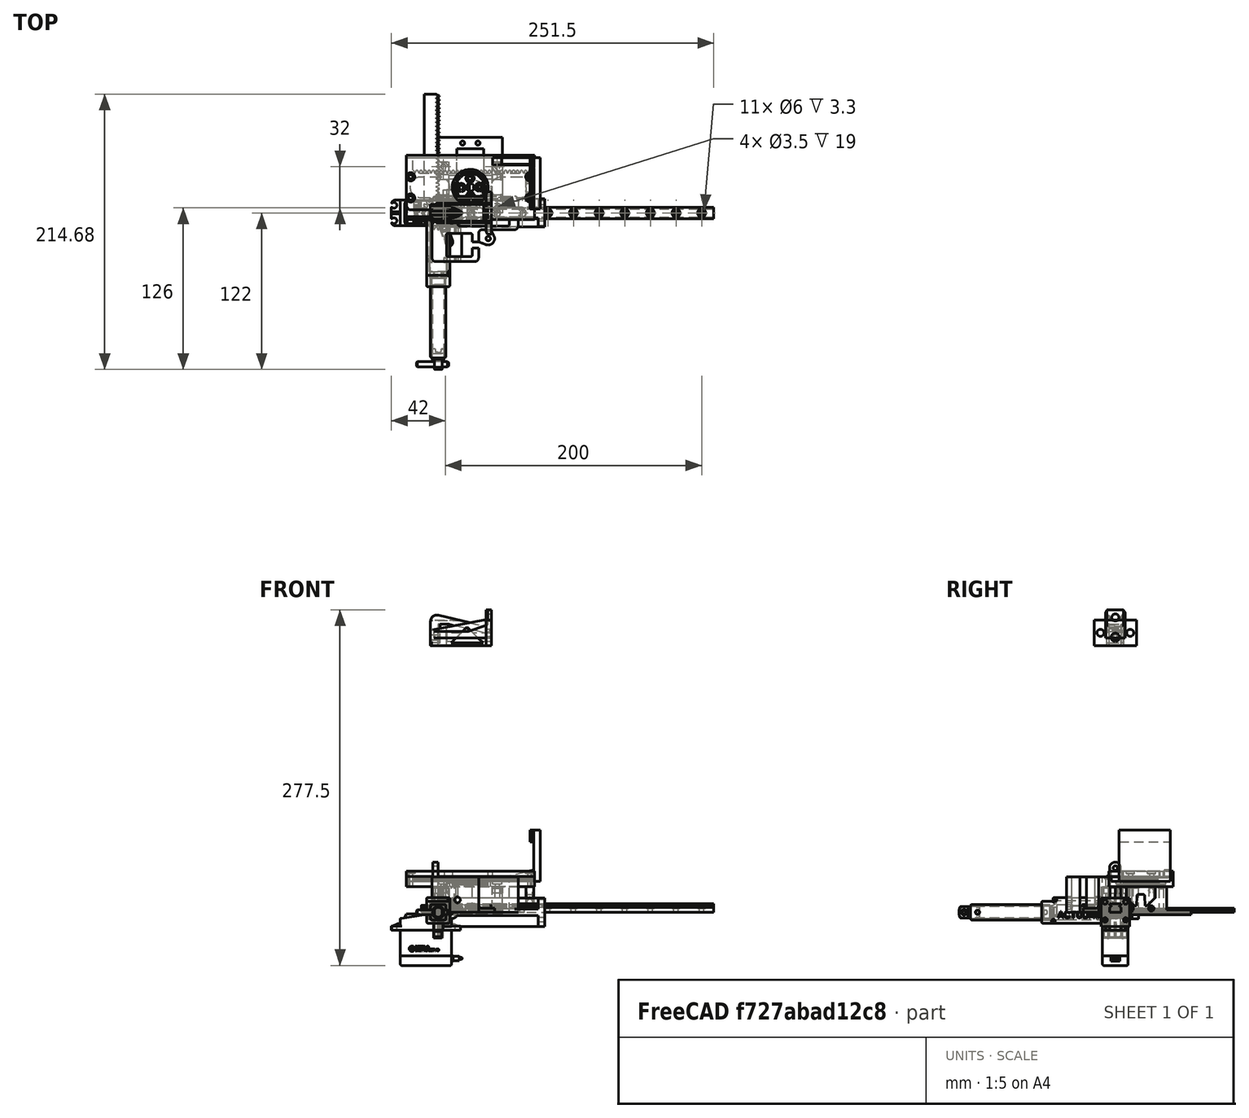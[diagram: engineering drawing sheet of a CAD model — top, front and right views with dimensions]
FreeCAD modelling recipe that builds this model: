
FCSTD DOCUMENT  (FreeCAD 1.0R39285 (Git))
Label: PincePlanche
License: All rights reserved
LicenseURL: https://en.wikipedia.org/wiki/All_rights_reserved
objects: Sketcher::SketchObject×61, PartDesign::Pocket×31, PartDesign::Pad×28, PartDesign::Body×17, App::FeaturePython×11, Part::Feature×9, Part::FeaturePython×8, PartDesign::Mirrored×7, App::Part×6, App::Link×3, PartDesign::Chamfer×2, Assembly::JointGroup×2, PartDesign::Revolution×2, PartDesign::PolarPattern×2, PartDesign::Fillet×2, PartDesign::FeatureBase×2, Assembly::AssemblyObject×2, PartDesign::LinearPattern×1, Spreadsheet::Sheet×1, PartDesign::MultiTransform×1, +2 more types
note: 380 computed .brp shape members not serialized (recipe doc carries the construction recipe); baked Part::Feature solids carry a one-line shape summary decoded from their .brp
EXTERNAL_REF file=Robot_CRLG.FCStd obj=Body073

FEATURE [Part::FeaturePython] InvoluteRack  # WARN: FeaturePython — macro-defined, semantics opaque (R4)
  AttacherType = Attacher::AttachEngine3D
  add_endings = true
  clearance = 0.25
  double_helix = false
  head = 0
  head_fillet = 0
  height = 3
  helix_angle = 0
  module = 1
  num_teeth = 30
  pressure_angle = 20
  properties_from_tool = false
  root_fillet = 0
  simplified = false
  thickness = 9.5
  transverse_pitch = 3.14159
  version = 1.3.0
FEATURE [Part::FeaturePython] InvoluteGear  # WARN: FeaturePython — macro-defined, semantics opaque (R4)
  AttacherType = Attacher::AttachEngine3D
  addendum_diameter = 26
  angular_backlash = 0
  axle_hole = false
  axle_holesize = 10
  backlash = 0
  clearance = 0.25
  double_helix = false
  head = 0
  head_fillet = 0
  height = 5.5
  helix_angle = 0
  module = 1
  num_teeth = 24
  numpoints = 20
  offset_hole = false
  offset_holeoffset = 10
  offset_holesize = 10
  pitch_diameter = 24
  pressure_angle = 20
  properties_from_tool = false
  reversed_backlash = false
  root_diameter = 21.5
  root_fillet = 0
  shift = 0
  simple = false
  transverse_pitch = 3.14159
  traverse_module = 1
  undercut = false
  version = 1.3.0
  expr: angular_backlash = backlash / pitch_diameter * 360 ° / pi
FEATURE [Part::Feature] Part__Feature008002002006397  label="chariot_MGN9-H"
  Placement = pos=(0,0,0) rot=(0.707107,0.707107,0;3.14159rad)
  shape: bbox 8.005 x 20.01 x 40.67 mm, 245 faces, 9 solids (baked)
FEATURE [Sketcher::SketchObject] Sketch031
  ArcFitTolerance = 0
  AttachmentSupport = -> [YZ_Plane013]
  FullyConstrained = true
  MakeInternals = false
  MapMode = 5
  Placement = pos=(0,0,0) rot=(0.57735,0.57735,0.57735;2.0944rad)
  sketch-geometry (4):
    g0: LineSegment StartX=-4.5 StartY=0 StartZ=0 EndX=4.5 EndY=0 EndZ=0
    g1: LineSegment StartX=4.5 StartY=0 StartZ=0 EndX=4.5 EndY=6.5 EndZ=0
    g2: LineSegment StartX=4.5 StartY=6.5 StartZ=0 EndX=-4.5 EndY=6.5 EndZ=0
    g3: LineSegment StartX=-4.5 StartY=6.5 StartZ=0 EndX=-4.5 EndY=0 EndZ=0
  constraints (11):
    c: Coincident(g0,g1)
    c: Coincident(g1,g2)
    c: Coincident(g2,g3)
    c: Coincident(g3,g0)
    c: Horizontal(g0)
    c: Horizontal(g2)
    c: Vertical(g1)
    c: Vertical(g3)
    c: Symmetric(g0,g0,g-1)
    c: DistanceX(g0,g0) = 9  'width'
    c: DistanceY(g1,g1) = 6.5  'height'
FEATURE [PartDesign::Pad] Pad012
  Direction = (1,0,0)
  Length = 215
  Length2 = 10
  Placement = pos=(0,0,0) rot=(0.57735,0.57735,0.57735;2.0944rad)
  Profile = -> Sketch031
  ReferenceAxis = -> Sketch031 [N_Axis]
  Suppressed = false
  Type = 0
  expr: Length = Spreadsheet001.length
FEATURE [Sketcher::SketchObject] Sketch032
  ArcFitTolerance = 0
  AttachmentSupport = -> [YZ_Plane013]
  FullyConstrained = true
  MakeInternals = false
  MapMode = 5
  Placement = pos=(0,0,0) rot=(0.57735,-0.57735,-0.57735;2.0944rad)
  expr: Constraints[13] = 6.5 - 1.8
  expr: Constraints[14] = <<Sketch031>>.Constraints.width / 2 + 0.1 mm
  sketch-geometry (10):
    g0: ArcOfCircle CenterX=-4.6 CenterY=4.7 CenterZ=0 NormalX=0 NormalY=0 NormalZ=1 AngleXU=0 Radius=1 StartAngle=0.25268 EndAngle=6.03051
    g1: LineSegment StartX=-3.63175 StartY=4.95 StartZ=0 EndX=-3.13175 EndY=4.95 EndZ=0
    g2: LineSegment StartX=-3.13175 StartY=4.95 StartZ=0 EndX=-3.13175 EndY=4.45 EndZ=0
    g3: LineSegment StartX=-3.13175 StartY=4.45 StartZ=0 EndX=-3.63175 EndY=4.45 EndZ=0
    g4: LineSegment [constr] StartX=-4.6 StartY=4.7 StartZ=0 EndX=-3.13175 EndY=4.7 EndZ=0
    g5: ArcOfCircle CenterX=4.6 CenterY=4.7 CenterZ=0 NormalX=0 NormalY=0 NormalZ=1 AngleXU=0 Radius=1 StartAngle=3.39427 EndAngle=9.1721
    g6: LineSegment StartX=3.63175 StartY=4.95 StartZ=0 EndX=3.13175 EndY=4.95 EndZ=0
    g7: LineSegment StartX=3.13175 StartY=4.95 StartZ=0 EndX=3.13175 EndY=4.45 EndZ=0
    g8: LineSegment StartX=3.13175 StartY=4.45 StartZ=0 EndX=3.63175 EndY=4.45 EndZ=0
    g9: LineSegment [constr] StartX=4.6 StartY=4.7 StartZ=0 EndX=3.13175 EndY=4.7 EndZ=0
  constraints (29):
    c: Horizontal(g1)
    c: Coincident(g2,g1)
    c: Vertical(g2)
    c: Coincident(g3,g2)
    c: Horizontal(g3)
    c: Coincident(g4,g0)
    c: Horizontal(g4)
    c: Symmetric(g2,g1,g4)
    c: Coincident(g0,g3)
    c: Coincident(g0,g1)
    c: DistanceY(g2,g2) = 0.5
    c: DistanceX(g1,g1) = 0.5
    c: Diameter(g0) = 2
    c: DistanceY(g-1,g0) = 4.7
    c: DistanceX(g0,g-1) = 4.6
    c: Horizontal(g6)
    c: Coincident(g7,g6)
    c: Vertical(g7)
    c: Coincident(g8,g7)
    c: Horizontal(g8)
    c: Coincident(g9,g5)
    c: Horizontal(g9)
    c: Symmetric(g7,g6,g9)
    c: Coincident(g5,g8)
    c: Coincident(g5,g6)
    c: Diameter(g5) = 2
    c: Symmetric(g4,g9,g-2)
    c: Equal(g2,g7)
    c: Equal(g1,g6)
FEATURE [PartDesign::Pocket] Pocket015  label="Balls cut"
  BaseFeature = -> Pad012
  Direction = (1,0,0)
  Length = 5
  Length2 = 5
  Placement = pos=(0,0,0) rot=(0.57735,0.57735,0.57735;2.0944rad)
  Profile = -> Sketch032
  ReferenceAxis = -> Sketch032 [N_Axis]
  Suppressed = false
  Type = 1
FEATURE [Sketcher::SketchObject] Sketch033
  ArcFitTolerance = 0
  AttachmentOffset = pos=(5.5,0,0) rot=(0,0,1;1.5708rad)
  AttachmentSupport = -> [XY_Plane013]
  FullyConstrained = true
  MakeInternals = false
  MapMode = 5
  Placement = pos=(5.5,0,0) rot=(0,0,1;1.5708rad)
  expr: .AttachmentOffset.Base.x = Spreadsheet001.offset
  sketch-geometry (1):
    g0: Circle CenterX=0 CenterY=0 CenterZ=0 NormalX=0 NormalY=0 NormalZ=1 AngleXU=0 Radius=1.75
  constraints (2):
    c: Coincident(g0,g-1)
    c: Diameter(g0) = 3.5
FEATURE [PartDesign::Pocket] Pocket016  label="Screw hole"
  BaseFeature = -> Pocket015
  Direction = (0,0,-1)
  Length = 5
  Length2 = 5
  Midplane = true
  Placement = pos=(0,0,0) rot=(0.57735,0.57735,0.57735;2.0944rad)
  Profile = -> Sketch033
  ReferenceAxis = -> Sketch033 [N_Axis]
  Suppressed = false
  Type = 1
FEATURE [Sketcher::SketchObject] Sketch034
  ArcFitTolerance = 0
  AttachmentOffset = pos=(5.5,0,6.5) rot=(0,0,1;1.5708rad)
  AttachmentSupport = -> [XY_Plane013]
  FullyConstrained = true
  MakeInternals = false
  MapMode = 5
  Placement = pos=(5.5,0,6.5) rot=(0,0,1;1.5708rad)
  expr: .AttachmentOffset.Base.x = Spreadsheet001.offset
  expr: .AttachmentOffset.Base.z = Sketch031.Constraints.height
  sketch-geometry (1):
    g0: Circle CenterX=0 CenterY=0 CenterZ=0 NormalX=0 NormalY=0 NormalZ=1 AngleXU=0 Radius=3
  constraints (2):
    c: Coincident(g0,g-1)
    c: Diameter(g0) = 6
FEATURE [PartDesign::Pocket] Pocket017  label="Screw head cut"
  BaseFeature = -> Pocket016
  Direction = (0,0,-1)
  Length = 3.5
  Length2 = 5
  Placement = pos=(0,0,0) rot=(0.57735,0.57735,0.57735;2.0944rad)
  Profile = -> Sketch034
  ReferenceAxis = -> Sketch034 [N_Axis]
  Suppressed = false
  Type = 0
FEATURE [PartDesign::Chamfer] Chamfer001  label="Chamfer"
  Angle = 45
  Base = -> Pocket017 [Edge47]
  BaseFeature = -> Pocket017
  ChamferType = 0
  FlipDirection = false
  Placement = pos=(0,0,0) rot=(0.57735,0.57735,0.57735;2.0944rad)
  Size = 0.2
  Size2 = 1
  SupportTransform = false
  Suppressed = false
  UseAllEdges = false
FEATURE [PartDesign::LinearPattern] LinearPattern001  label="LinearPattern"
  BaseFeature = -> Chamfer001
  Direction = -> Sketch033 [V_Axis]
  Length = 200
  Mode = 0
  Occurrences = 11
  Offset = 20
  Originals = -> [Pocket016,Pocket017,Chamfer001]
  Placement = pos=(0,0,0) rot=(0.57735,0.57735,0.57735;2.0944rad)
  Reversed = true
  Suppressed = false
  TransformMode = 0
  expr: Length = Spreadsheet001.distance
  expr: Occurrences = Spreadsheet001.holes_number
FEATURE [PartDesign::Body] Body011  label="Hiwin rail MGN9R"
  AllowCompound = false
  Group = -> [Sketch031,Pad012,Sketch032,Pocket015,Sketch033,Pocket016,Sketch034,Pocket017,Chamfer001,LinearPattern001]
  Origin = -> Origin013
  Tip = -> LinearPattern001
FEATURE [Spreadsheet::Sheet] Spreadsheet001  label="Spreadsheet_MGN9"
  cells = A1='Length rail; B1='Длина рельсы, мм; C1(length)=215; A2='Holes distance; B2='Расстояние между отверстиями; C2(holes_distance)=20; A3='Holes number; B3='Количество отверстий; C3(holes_number)==floor((length - min_offset * 2) / holes_distance) + 2; A4='Distance end holes; B4='Расстояние между центрами крайних отверстий; C4(distance)==holes_distance * (holes_number - 1); A5='Offset 1st hole; B5='Позиция 1го отверстия; C5(offset)=5.5; A6='Min offset 1st hole; B6='Минимальное расстояние от края до центра 1го отверстия; C6(min_offset)=9
FEATURE [App::Part] Part002002  label="Hiwin MGN9"
  Group = -> [Body011,Spreadsheet001]
  Origin = -> Origin014
  Placement = pos=(0,0,220) rot=(0,1,0;1.5708rad)
FEATURE [Assembly::JointGroup] Joints001
FEATURE [Part::Feature] Part__Feature008002002006398  label="L16_50MM_BODY_A"
  Placement = pos=(0,-51,0) rot=(0,0,1;0rad)
  shape: bbox 20.08 x 117.7 x 20.17 mm, 719 faces (baked)
FEATURE [Part::Feature] Part__Feature008002002006399  label="L16_50MM_LIFT_A"
  Placement = pos=(0,-51,0) rot=(0,0,1;0rad)
  shape: bbox 10.2 x 71.63 x 9.971 mm, 40 faces (baked)
  expr: .Placement.Base.y = -51 mm - VarSet.Position_verrin
FEATURE [Sketcher::SketchObject] Sketch036
  ArcFitTolerance = 1e-06
  AttachmentSupport = -> [YZ_Plane017]
  FullyConstrained = true
  MakeInternals = false
  MapMode = 5
  Placement = pos=(0,0,0) rot=(0.57735,0.57735,0.57735;2.0944rad)
  sketch-geometry (4):
    g0: LineSegment StartX=-11 StartY=11 StartZ=0 EndX=-11 EndY=-11 EndZ=0
    g1: LineSegment StartX=-11 StartY=-11 StartZ=0 EndX=11 EndY=-11 EndZ=0
    g2: LineSegment StartX=11 StartY=-11 StartZ=0 EndX=11 EndY=11 EndZ=0
    g3: LineSegment StartX=11 StartY=11 StartZ=0 EndX=-11 EndY=11 EndZ=0
  constraints (11):
    c: Coincident(g0,g1)
    c: Coincident(g1,g2)
    c: Coincident(g2,g3)
    c: Coincident(g3,g0)
    c: Vertical(g0)
    c: Vertical(g2)
    c: Horizontal(g1)
    c: Horizontal(g3)
    c: Symmetric(g2,g0,g-1)
    c: DistanceX(g3,g3) = 22
    c: DistanceY(g0,g0) = 22
FEATURE [Sketcher::SketchObject] Sketch037
  ArcFitTolerance = 1e-06
  AttachmentOffset = pos=(0,0,74) rot=(0,0,1;0rad)
  AttachmentSupport = -> [YZ_Plane017]
  FullyConstrained = true
  MakeInternals = false
  MapMode = 5
  Placement = pos=(74,0,0) rot=(0.57735,0.57735,0.57735;2.0944rad)
  sketch-geometry (4):
    g0: LineSegment StartX=-4 StartY=11 StartZ=0 EndX=-4 EndY=-11 EndZ=0
    g1: LineSegment StartX=-4 StartY=-11 StartZ=0 EndX=4 EndY=-11 EndZ=0
    g2: LineSegment StartX=4 StartY=-11 StartZ=0 EndX=4 EndY=11 EndZ=0
    g3: LineSegment StartX=4 StartY=11 StartZ=0 EndX=-4 EndY=11 EndZ=0
  constraints (11):
    c: Coincident(g0,g1)
    c: Coincident(g1,g2)
    c: Coincident(g2,g3)
    c: Coincident(g3,g0)
    c: Vertical(g0)
    c: Vertical(g2)
    c: Horizontal(g1)
    c: Horizontal(g3)
    c: Symmetric(g2,g0,g-1)
    c: DistanceY(g2,g2) = 22
    c: Distance(g1,g1) = 8
FEATURE [Sketcher::SketchObject] Sketch038
  ArcFitTolerance = 1e-06
  AttachmentSupport = -> [YZ_Plane017]
  FullyConstrained = true
  MakeInternals = false
  MapMode = 5
  Placement = pos=(0,0,0) rot=(0.57735,0.57735,0.57735;2.0944rad)
  sketch-geometry (1):
    g0: Circle CenterX=7.5 CenterY=-8 CenterZ=0 NormalX=0 NormalY=0 NormalZ=1 AngleXU=0 Radius=1.75
  constraints (3):
    c: Diameter(g0) = 3.5
    c: DistanceX(g-1,g0) = 7.5
    c: DistanceY(g0,g-1) = 8
FEATURE [PartDesign::Pad] Pad013
  Direction = (1,0,0)
  Length = 6.5
  Length2 = 10
  Placement = pos=(0,0,0) rot=(1,1,1;2.0944rad)
  Profile = -> Sketch036
  ReferenceAxis = -> Sketch036 [N_Axis]
  Suppressed = false
  Type = 0
FEATURE [PartDesign::Pocket] Pocket018
  BaseFeature = -> Pad013
  Direction = (-1,0,0)
  Length = 5
  Length2 = 5
  Midplane = true
  Placement = pos=(0,0,0) rot=(1,1,1;2.0944rad)
  Profile = -> Sketch038
  ReferenceAxis = -> Sketch038 [N_Axis]
  Suppressed = false
  Type = 1
FEATURE [PartDesign::Mirrored] Mirrored002
  MirrorPlane = -> Sketch038 [V_Axis]
  Placement = pos=(0,0,0) rot=(1,1,1;2.0944rad)
  Suppressed = false
  TransformMode = 0
FEATURE [PartDesign::Mirrored] Mirrored003
  MirrorPlane = -> Sketch038 [H_Axis]
  Placement = pos=(0,0,0) rot=(1,1,1;2.0944rad)
  Suppressed = false
  TransformMode = 0
FEATURE [PartDesign::MultiTransform] MultiTransform
  BaseFeature = -> Pocket018
  Originals = -> [Pocket018]
  Placement = pos=(0,0,0) rot=(1,1,1;2.0944rad)
  Suppressed = false
  TransformMode = 0
  Transformations = -> [Mirrored002,Mirrored003]
FEATURE [Sketcher::SketchObject] Sketch040
  ArcFitTolerance = 1e-06
  AttachmentOffset = pos=(0,0,6.5) rot=(0,0,1;0rad)
  AttachmentSupport = -> [YZ_Plane017]
  FullyConstrained = true
  MakeInternals = false
  MapMode = 5
  Placement = pos=(6.5,0,0) rot=(0.57735,0.57735,0.57735;2.0944rad)
  sketch-geometry (4):
    g0: LineSegment StartX=-4 StartY=11 StartZ=0 EndX=-4 EndY=-11 EndZ=0
    g1: LineSegment StartX=-4 StartY=-11 StartZ=0 EndX=4 EndY=-11 EndZ=0
    g2: LineSegment StartX=4 StartY=-11 StartZ=0 EndX=4 EndY=11 EndZ=0
    g3: LineSegment StartX=4 StartY=11 StartZ=0 EndX=-4 EndY=11 EndZ=0
  constraints (11):
    c: Coincident(g0,g1)
    c: Coincident(g1,g2)
    c: Coincident(g2,g3)
    c: Coincident(g3,g0)
    c: Vertical(g0)
    c: Vertical(g2)
    c: Horizontal(g1)
    c: Horizontal(g3)
    c: Symmetric(g2,g0,g-1)
    c: DistanceX(g3,g3) = 8
    c: DistanceY(g2,g2) = 22
FEATURE [PartDesign::AdditiveLoft] AdditiveLoft
  BaseFeature = -> MultiTransform
  Closed = false
  Placement = pos=(0,0,0) rot=(1,1,1;2.0944rad)
  Profile = -> Sketch037
  Ruled = false
  Sections = -> [Sketch040]
  Suppressed = false
FEATURE [Sketcher::SketchObject] Sketch041
  ArcFitTolerance = 1e-06
  AttachmentOffset = pos=(0,1,0) rot=(0,0,1;0rad)
  AttachmentSupport = -> [AdditiveLoft]
  FullyConstrained = true
  MakeInternals = false
  MapMode = 5
  Placement = pos=(74,0,1) rot=(0.57735,0.57735,0.57735;2.0944rad)
  sketch-geometry (8):
    g0: LineSegment StartX=-11 StartY=10 StartZ=0 EndX=-11 EndY=-10 EndZ=0
    g1: LineSegment StartX=-11 StartY=-10 StartZ=0 EndX=11 EndY=-10 EndZ=0
    g2: LineSegment StartX=11 StartY=-10 StartZ=0 EndX=11 EndY=10 EndZ=0
    g3: LineSegment StartX=11 StartY=10 StartZ=0 EndX=-11 EndY=10 EndZ=0
    g4: Circle CenterX=8 CenterY=-7 CenterZ=0 NormalX=0 NormalY=0 NormalZ=1 AngleXU=0 Radius=1.75
    g5: Circle CenterX=-8 CenterY=-7 CenterZ=0 NormalX=0 NormalY=0 NormalZ=1 AngleXU=0 Radius=1.75
    g6: Circle CenterX=8 CenterY=7 CenterZ=0 NormalX=0 NormalY=0 NormalZ=1 AngleXU=0 Radius=1.75
    g7: Circle CenterX=-8 CenterY=7 CenterZ=0 NormalX=0 NormalY=0 NormalZ=1 AngleXU=0 Radius=1.75
  constraints (21):
    c: Coincident(g0,g1)
    c: Coincident(g1,g2)
    c: Coincident(g2,g3)
    c: Coincident(g3,g0)
    c: Vertical(g0)
    c: Vertical(g2)
    c: Horizontal(g1)
    c: Distance(g1,g1) = 22
    c: Symmetric(g0,g1,g-1)
    c: Horizontal(g3)
    c: DistanceY(g2,g2) = 20
    c: Diameter(g4) = 3.5
    c: Diameter(g5) = 3.5
    c: Diameter(g6) = 3.5
    c: Diameter(g7) = 3.5
    c: Symmetric(g7,g4,g-1)
    c: Symmetric(g5,g6,g-1)
    c: Horizontal(g6,g7)
    c: Vertical(g7,g5)
    c: DistanceX(g7,g-1) = 8
    c: DistanceY(g-1,g7) = 7
FEATURE [PartDesign::Pad] Pad014
  BaseFeature = -> AdditiveLoft
  Direction = (1,0,0)
  Length = 5
  Length2 = 10
  Placement = pos=(0,0,0) rot=(1,1,1;2.0944rad)
  Profile = -> Sketch041
  ReferenceAxis = -> Sketch041 [N_Axis]
  Suppressed = false
  Type = 0
FEATURE [Sketcher::SketchObject] Sketch042
  ArcFitTolerance = 1e-06
  AttachmentSupport = -> [XY_Plane019]
  FullyConstrained = true
  MakeInternals = false
  MapMode = 5
  Placement = pos=(0,0,0) rot=(0,1,0;3.14159rad)
  expr: Constraints[36] = 20 mm + VarSet.jeu
  expr: Constraints[37] = 40 mm + VarSet.jeu
  expr: Constraints[72] = 18 mm + VarSet.jeu
  expr: Constraints[73] = 20 mm + VarSet.jeu
  expr: Constraints[86] = 9 mm + VarSet.jeu
  expr: Constraints[87] = 6.5 mm + VarSet.jeu
  sketch-geometry (52):
    g0: LineSegment StartX=-28.5 StartY=-38 StartZ=0 EndX=1.8 EndY=-38 EndZ=0
    g1: LineSegment StartX=4.8 StartY=-35 StartZ=0 EndX=4.8 EndY=10 EndZ=0
    g2: ArcOfCircle CenterX=1.8 CenterY=-35 CenterZ=0 NormalX=0 NormalY=0 NormalZ=1 AngleXU=0 Radius=3 StartAngle=4.71239 EndAngle=6.28319
    g3: ArcOfCircle CenterX=1.8 CenterY=10 CenterZ=0 NormalX=0 NormalY=0 NormalZ=1 AngleXU=0 Radius=3 StartAngle=0 EndAngle=1.5708
    g4: GeomPoint [constr] X=4.8 Y=-38 Z=0
    g5: LineSegment StartX=-59.5 StartY=-13 StartZ=0 EndX=-34.5 EndY=-13 EndZ=0
    g6: LineSegment StartX=1.8 StartY=13 StartZ=0 EndX=-59.5 EndY=13 EndZ=0
    g7: ArcOfCircle CenterX=-59.5 CenterY=10 CenterZ=0 NormalX=0 NormalY=0 NormalZ=1 AngleXU=0 Radius=3 StartAngle=1.5708 EndAngle=3.14159
    g8: ArcOfCircle CenterX=-59.5 CenterY=-10 CenterZ=0 NormalX=0 NormalY=0 NormalZ=1 AngleXU=0 Radius=3 StartAngle=3.14159 EndAngle=4.71239
    g9: LineSegment StartX=-54.575 StartY=-10.075 StartZ=0 EndX=-16.425 EndY=-10.075 EndZ=0
    g10: LineSegment StartX=-15.425 StartY=-9.075 StartZ=0 EndX=-15.425 EndY=9.075 EndZ=0
    g11: LineSegment StartX=-16.425 StartY=10.075 StartZ=0 EndX=-54.575 EndY=10.075 EndZ=0
    g12: ArcOfCircle CenterX=-54.575 CenterY=9.075 CenterZ=0 NormalX=0 NormalY=0 NormalZ=1 AngleXU=0 Radius=1 StartAngle=1.5708 EndAngle=3.14159
    g13: ArcOfCircle CenterX=-54.575 CenterY=-9.075 CenterZ=0 NormalX=0 NormalY=0 NormalZ=1 AngleXU=0 Radius=1 StartAngle=3.14159 EndAngle=4.71239
    g14: ArcOfCircle CenterX=-16.425 CenterY=-9.075 CenterZ=0 NormalX=0 NormalY=0 NormalZ=1 AngleXU=0 Radius=1 StartAngle=4.71239 EndAngle=6.28319
    g15: ArcOfCircle CenterX=-16.425 CenterY=9.075 CenterZ=0 NormalX=0 NormalY=0 NormalZ=1 AngleXU=0 Radius=1 StartAngle=0 EndAngle=1.5708
    g16: GeomPoint [constr] X=-55.575 Y=10.075 Z=0
    g17: GeomPoint [constr] X=-15.425 Y=-10.075 Z=0
    g18: GeomPoint X=-35.5 Y=0 Z=0
    g19: ArcOfCircle CenterX=-34.5 CenterY=-16 CenterZ=0 NormalX=0 NormalY=0 NormalZ=1 AngleXU=0 Radius=3 StartAngle=0 EndAngle=1.5708
    g20: LineSegment StartX=-31.5 StartY=-16 StartZ=0 EndX=-31.5 EndY=-22.5 EndZ=0
    g21: ArcOfCircle CenterX=-28.5 CenterY=-35 CenterZ=0 NormalX=0 NormalY=0 NormalZ=1 AngleXU=0 Radius=3 StartAngle=3.14159 EndAngle=4.71239
    g22: GeomPoint [constr] X=-31.5 Y=-38 Z=0
    g23: GeomPoint X=-16.5 Y=-25 Z=0
    g24: LineSegment StartX=-26.575 StartY=-17.125 StartZ=0 EndX=-26.575 EndY=-22.5 EndZ=0
    g25: LineSegment StartX=-25.375 StartY=-34.075 StartZ=0 EndX=-7.625 EndY=-34.075 EndZ=0
    g26: LineSegment StartX=-6.425 StartY=-32.875 StartZ=0 EndX=-6.425 EndY=-17.125 EndZ=0
    g27: LineSegment StartX=-7.625 StartY=-15.925 StartZ=0 EndX=-25.375 EndY=-15.925 EndZ=0
    g28: ArcOfCircle CenterX=-25.375 CenterY=-17.125 CenterZ=0 NormalX=0 NormalY=0 NormalZ=1 AngleXU=0 Radius=1.2 StartAngle=1.5708 EndAngle=3.14159
    g29: ArcOfCircle CenterX=-25.375 CenterY=-32.875 CenterZ=0 NormalX=0 NormalY=0 NormalZ=1 AngleXU=0 Radius=1.2 StartAngle=3.14159 EndAngle=4.71239
    g30: ArcOfCircle CenterX=-7.625 CenterY=-32.875 CenterZ=0 NormalX=0 NormalY=0 NormalZ=1 AngleXU=0 Radius=1.2 StartAngle=4.71239 EndAngle=6.28319
    g31: ArcOfCircle CenterX=-7.625 CenterY=-17.125 CenterZ=0 NormalX=0 NormalY=0 NormalZ=1 AngleXU=0 Radius=1.2 StartAngle=-9e-16 EndAngle=1.5708
    g32: GeomPoint [constr] X=-26.575 Y=-15.925 Z=0
    g33: GeomPoint [constr] X=-6.425 Y=-34.075 Z=0
    g34: LineSegment StartX=-6.575 StartY=4.575 StartZ=0 EndX=-6.575 EndY=-4.575 EndZ=0
    g35: LineSegment StartX=-6.575 StartY=-4.575 StartZ=0 EndX=0.075 EndY=-4.575 EndZ=0
    g36: LineSegment StartX=0.075 StartY=-4.575 StartZ=0 EndX=0.075 EndY=4.575 EndZ=0
    g37: LineSegment StartX=0.075 StartY=4.575 StartZ=0 EndX=-6.575 EndY=4.575 EndZ=0
    g38: GeomPoint X=-3.25 Y=0 Z=0
    g39: LineSegment StartX=-26.575 StartY=-22.5 StartZ=0 EndX=-31.5 EndY=-22.5 EndZ=0
    g40: LineSegment StartX=-31.5 StartY=-27.5 StartZ=0 EndX=-26.575 EndY=-27.5 EndZ=0
    g41: LineSegment StartX=-26.575 StartY=-27.5 StartZ=0 EndX=-26.575 EndY=-32.875 EndZ=0
    g42: LineSegment StartX=-31.5 StartY=-27.5 StartZ=0 EndX=-31.5 EndY=-35 EndZ=0
    g43: LineSegment [constr] StartX=-16.5 StartY=-25 StartZ=0 EndX=-31.5 EndY=-25 EndZ=0
    g44: LineSegment StartX=-62.5 StartY=4 StartZ=0 EndX=-55.575 EndY=4 EndZ=0
    g45: LineSegment StartX=-62.5 StartY=-4 StartZ=0 EndX=-55.575 EndY=-4 EndZ=0
    g46: LineSegment StartX=-55.575 StartY=-4 StartZ=0 EndX=-55.575 EndY=-9.075 EndZ=0
    g47: LineSegment StartX=-62.5 StartY=-4 StartZ=0 EndX=-62.5 EndY=-10 EndZ=0
    g48: LineSegment StartX=-62.5 StartY=10 StartZ=0 EndX=-62.5 EndY=4 EndZ=0
    g49: LineSegment StartX=-55.575 StartY=9.075 StartZ=0 EndX=-55.575 EndY=4 EndZ=0
    g50: Circle CenterX=-10.5 CenterY=6 CenterZ=0 NormalX=0 NormalY=0 NormalZ=1 AngleXU=0 Radius=1.75
    g51: Circle CenterX=-10.5 CenterY=-6 CenterZ=0 NormalX=0 NormalY=0 NormalZ=1 AngleXU=0 Radius=1.75
  constraints (130):
    c: Tangent(g0,g2) = -1.5708
    c: Tangent(g1,g2) = -1.5708
    c: Tangent(g1,g3) = -1.5708
    c: Vertical(g1)
    c: Horizontal(g0)
    c: Equal(g2,g3)
    c: PointOnObject(g4,g0)
    c: PointOnObject(g4,g1)
    c: DistanceX(g-1,g1) = 4.8
    c: Tangent(g5,g8) = -1.5708
    c: Tangent(g6,g7) = -1.5708
    c: Horizontal(g5)
    c: Horizontal(g6)
    c: Equal(g7,g8)
    c: DistanceY(g5,g6) = 26
    c: Symmetric(g7,g47,g-1)
    c: Radius(g7) = 3
    c: Tangent(g3,g6) = -1.5708
    c: Tangent(g9,g13) = -1.5708
    c: Tangent(g9,g14) = -1.5708
    c: Tangent(g10,g14) = -1.5708
    c: Tangent(g10,g15) = -1.5708
    c: Tangent(g11,g15) = -1.5708
    c: Tangent(g11,g12) = -1.5708
    c: Vertical(g10)
    c: Horizontal(g9)
    c: Horizontal(g11)
    c: Equal(g12,g13)
    c: Equal(g13,g14)
    c: Equal(g14,g15)
    c: PointOnObject(g16,g11)
    c: PointOnObject(g17,g9)
    c: PointOnObject(g17,g10)
    c: Radius(g13) = 1
    c: PointOnObject(g18,g-1)
    c: Symmetric(g16,g17,g18)
    c: DistanceY(g9,g11) = 20.15
    c: DistanceX(g12,g10) = 40.15
    c: DistanceX(g18,g-1) = 35.5
    c: DistanceX(g7,g18) = 27
    c: Vertical(g20)
    c: PointOnObject(g22,g42)
    c: PointOnObject(g22,g0)
    c: Tangent(g0,g21) = -1.5708
    c: Tangent(g19,g5) = 1.5708
    c: Tangent(g20,g19) = 1.5708
    c: DistanceY(g23,g-1) = 25
    c: DistanceX(g23,g-1) = 16.5
    c: DistanceX(g19,g23) = 15
    c: DistanceY(g0,g23) = 13
    c: Equal(g21,g19)
    c: Equal(g19,g2)
    c: Equal(g3,g7)
    c: Tangent(g24,g28) = -1.5708
    c: Tangent(g25,g29) = -1.5708
    c: Tangent(g25,g30) = -1.5708
    c: Tangent(g26,g30) = -1.5708
    c: Tangent(g26,g31) = -1.5708
    c: Tangent(g27,g31) = -1.5708
    c: Tangent(g27,g28) = -1.5708
    c: Vertical(g24)
    c: Vertical(g26)
    c: Horizontal(g25)
    c: Horizontal(g27)
    c: Equal(g28,g29)
    c: Equal(g29,g30)
    c: Equal(g30,g31)
    c: PointOnObject(g32,g24)
    c: PointOnObject(g32,g27)
    c: PointOnObject(g33,g25)
    c: PointOnObject(g33,g26)
    c: Symmetric(g33,g32,g23)
    c: DistanceY(g25,g27) = 18.15
    c: DistanceX(g24,g26) = 20.15
    c: Radius(g31) = 1.2
    c: Coincident(g34,g35)
    c: Coincident(g35,g36)
    c: Coincident(g36,g37)
    c: Coincident(g37,g34)
    c: Vertical(g34)
    c: Vertical(g36)
    c: Horizontal(g35)
    c: Horizontal(g37)
    c: PointOnObject(g38,g-1)
    c: Symmetric(g36,g34,g38)
    c: DistanceX(g38,g-1) = 3.25
    c: DistanceY(g34,g34) = 9.15
    c: DistanceX(g37,g37) = 6.65
    c: Horizontal(g39)
    c: Horizontal(g40)
    c: PointOnObject(g40,g41)
    c: PointOnObject(g40,g42)
    c: Coincident(g24,g39)
    c: PointOnObject(g41,g40)
    c: Coincident(g20,g39)
    c: PointOnObject(g42,g40)
    c: Coincident(g43,g23)
    c: Horizontal(g43)
    c: Symmetric(g20,g40,g43)
    c: Vertical(g24,g40)
    c: Vertical(g40,g20)
    c: DistanceY(g40,g24) = 5
    c: Vertical(g41)
    c: Tangent(g41,g29) = -1.5708
    c: Tangent(g42,g21) = -1.5708
    c: Vertical(g42)
    c: Horizontal(g44)
    c: PointOnObject(g45,g47)
    c: Horizontal(g45)
    c: PointOnObject(g45,g46)
    c: PointOnObject(g46,g45)
    c: PointOnObject(g47,g45)
    c: Coincident(g48,g44)
    c: Vertical(g48)
    c: Tangent(g7,g48) = -1.5708
    c: Tangent(g47,g8) = -1.5708
    c: Tangent(g46,g13) = -1.5708
    c: Vertical(g46)
    c: Vertical(g47)
    c: Coincident(g49,g44)
    c: Vertical(g49)
    c: Tangent(g49,g12) = -1.5708
    c: Symmetric(g44,g45,g-1)
    c: Vertical(g16,g12)
    c: DistanceY(g45,g44) = 8
    c: Symmetric(g50,g51,g-1)
    c: DistanceX(g18,g51) = 25
    c: DistanceY(g18,g50) = 6
    c: Equal(g50,g51)
    c: Diameter(g50) = 3.5
FEATURE [PartDesign::Pad] Pad015
  Direction = (0,0,-1)
  Length = 27.5
  Length2 = 10
  Profile = -> Sketch042
  ReferenceAxis = -> Sketch042 [N_Axis]
  Reversed = true
  Suppressed = false
  Type = 0
FEATURE [Sketcher::SketchObject] Sketch043
  ArcFitTolerance = 1e-06
  AttachmentSupport = -> [XZ_Plane017]
  FullyConstrained = true
  MakeInternals = false
  MapMode = 5
  Placement = pos=(0,0,0) rot=(1,0,0;1.5708rad)
  sketch-geometry (4):
    g0: ArcOfCircle CenterX=6.5 CenterY=0 CenterZ=0 NormalX=0 NormalY=0 NormalZ=1 AngleXU=0 Radius=5 StartAngle=4.71239 EndAngle=7.85398
    g1: LineSegment StartX=6.5 StartY=5 StartZ=0 EndX=0 EndY=5 EndZ=0
    g2: LineSegment StartX=0 StartY=5 StartZ=0 EndX=0 EndY=-5 EndZ=0
    g3: LineSegment StartX=0 StartY=-5 StartZ=0 EndX=6.5 EndY=-5 EndZ=0
  constraints (11):
    c: PointOnObject(g0,g-1)
    c: Coincident(g1,g2)
    c: Coincident(g2,g3)
    c: Horizontal(g1)
    c: Horizontal(g3)
    c: Vertical(g2)
    c: PointOnObject(g2,g-2)
    c: Tangent(g0,g3) = -1.5708
    c: Tangent(g1,g0) = -1.5708
    c: DistanceX(g1,g1) = 6.5
    c: DistanceY(g2,g2) = 10
FEATURE [PartDesign::Pad] Pad016
  BaseFeature = -> Pad014
  Direction = (0,-1,2e-16)
  Length = 22
  Length2 = 10
  Midplane = true
  Placement = pos=(0,0,0) rot=(1,1,1;2.0944rad)
  Profile = -> Sketch043
  ReferenceAxis = -> Sketch043 [N_Axis]
  Suppressed = false
  Type = 0
FEATURE [Part::FeaturePython] ThreadedRod  label="M4x25-Tige filetée"  # WARN: FeaturePython — macro-defined, semantics opaque (R4)
  Diameter = 6
  DiameterCustom = 6
  Invert = false
  LeftHanded = false
  Length = 25
  MatchOuter = false
  OffsetAngle = 0
  PitchCustom = 1
  Placement = pos=(8,-118,0) rot=(0,1,0;1.5708rad)
  Thread = false
  Type = 4
  expr: .Placement.Base.y = -118 mm - VarSet.Position_verrin
FEATURE [App::Part] L16_50MM_SW_ASM
  Group = -> [Part__Feature008002002006398,Part__Feature008002002006399,ThreadedRod]
  Origin = -> Origin018
  Placement = pos=(15,-25,9.5) rot=(0.57735,-0.57735,0.57735;4.18879rad)
FEATURE [Sketcher::SketchObject] Sketch044
  ArcFitTolerance = 1e-06
  AttachmentSupport = -> [XZ_Plane017]
  FullyConstrained = true
  MakeInternals = false
  MapMode = 5
  Placement = pos=(0,0,0) rot=(1,0,0;1.5708rad)
  sketch-geometry (1):
    g0: Circle CenterX=5 CenterY=0 CenterZ=0 NormalX=0 NormalY=0 NormalZ=1 AngleXU=0 Radius=2.25
  constraints (3):
    c: Diameter(g0) = 4.5
    c: PointOnObject(g0,g-1)
    c: Distance(g0,g-2) = 5
FEATURE [PartDesign::Pocket] Pocket019
  BaseFeature = -> Pad016
  Direction = (0,1,-2e-16)
  Length = 5
  Length2 = 5
  Midplane = true
  Placement = pos=(0,0,0) rot=(1,1,1;2.0944rad)
  Profile = -> Sketch044
  ReferenceAxis = -> Sketch044 [N_Axis]
  Suppressed = false
  Type = 1
FEATURE [Part::FeaturePython] Screw001  label="M3x10-Vis"  # WARN: FeaturePython — macro-defined, semantics opaque (R4)
  Diameter = 4
  Invert = false
  LeftHanded = false
  Length = 10
  LengthCustom = 10
  MatchOuter = false
  OffsetAngle = 0
  Placement = pos=(11,-7.5,8) rot=(0,-1,0;4.71239rad)
  Thread = false
  Type = 75
FEATURE [PartDesign::Pad] Pad018
  BaseFeature = -> Pocket019
  Direction = (3e-16,-1e-15,-1)
  Length = 2
  Length2 = 10
  Placement = pos=(0,0,0) rot=(1,1,1;2.0944rad)
  Profile = -> Pocket019 [Face32]
  Suppressed = false
  Type = 0
FEATURE [Sketcher::SketchObject] Sketch045
  ArcFitTolerance = 1e-06
  AttachmentSupport = -> [XZ_Plane017]
  ExternalGeometry = -> [Sketch041,Pad018]
  FullyConstrained = true
  MakeInternals = false
  MapMode = 5
  Placement = pos=(0,0,0) rot=(1,0,0;1.5708rad)
  sketch-geometry (4):
    g0: LineSegment StartX=9 StartY=2.5 StartZ=0 EndX=9 EndY=-2.5 EndZ=0
    g1: LineSegment StartX=9 StartY=-2.5 StartZ=0 EndX=74 EndY=-2.5 EndZ=0
    g2: LineSegment StartX=74 StartY=-2.5 StartZ=0 EndX=74 EndY=2.5 EndZ=0
    g3: LineSegment StartX=74 StartY=2.5 StartZ=0 EndX=9 EndY=2.5 EndZ=0
  constraints (11):
    c: Coincident(g0,g1)
    c: Coincident(g1,g2)
    c: Coincident(g2,g3)
    c: Coincident(g3,g0)
    c: Vertical(g0)
    c: Horizontal(g1)
    c: Horizontal(g3)
    c: Vertical(g2,g-3)
    c: Symmetric(g2,g1,g-1)
    c: DistanceY(g0,g0) = 5
    c: DistanceX(g-1,g0) = 9
FEATURE [PartDesign::Pad] Pad017
  BaseFeature = -> Pad018
  Direction = (0,-1,2e-16)
  Length = 22
  Length2 = 10
  Midplane = true
  Placement = pos=(0,0,0) rot=(1,1,1;2.0944rad)
  Profile = -> Sketch045
  ReferenceAxis = -> Sketch045 [N_Axis]
  Suppressed = false
  Type = 0
FEATURE [App::Link] Link003  label="Plaque_AR_chassis"
  LinkPlacement = pos=(18.823,2.146e-06,-2) rot=(0,0,1;1.5708rad)
  LinkedObject = -> <external Robot_CRLG.FCStd>#Body073
  Placement = pos=(18.823,2.146e-06,-2) rot=(0,0,1;1.5708rad)
FEATURE [App::VarSet] VarSet
  Position_verrin = 0
  jeu = 0.15
FEATURE [Part::Feature] Part__Feature008002002006400  label="Lever 25T001"
  Placement = pos=(0,0,0) rot=(-1,0,0;1.5708rad)
  shape: bbox 18.84 x 33.03 x 6.019 mm, 125 faces (baked)
FEATURE [Part::Feature] Part__Feature008002002006401  label="Axis Servo001"
  Placement = pos=(0,0,0) rot=(-1,0,0;1.5708rad)
  shape: bbox 5 x 5 x 8 mm, 5 faces (baked)
FEATURE [Part::Feature] Part__Feature008002002006402  label="Servo DS3218MG001"
  Placement = pos=(0,0,0) rot=(-1,0,0;1.5708rad)
  shape: bbox 55 x 20 x 41 mm, 772 faces (baked)
FEATURE [Part::FeaturePython] Screw004  label="M2x5-Vis"  # WARN: FeaturePython — macro-defined, semantics opaque (R4)
  BaseObject = -> Body014 [Edge6]
  Diameter = 2
  Invert = true
  LeftHanded = false
  Length = 10
  LengthCustom = 5
  MatchOuter = false
  OffsetAngle = 0
  Placement = pos=(0,1e-15,4.8) rot=(0,0,1;0rad)
  Thread = false
  Type = 76
FEATURE [Sketcher::SketchObject] Sketch048
  ArcFitTolerance = 0
  AttachmentSupport = -> [XZ_Plane021]
  FullyConstrained = true
  MakeInternals = false
  MapMode = 5
  Placement = pos=(0,0,0) rot=(1,0,0;1.5708rad)
  expr: Constraints[19] = 19.8 / 2
  sketch-geometry (8):
    g0: LineSegment StartX=2.5 StartY=3.4 StartZ=0 EndX=2.5 EndY=0 EndZ=0
    g1: LineSegment StartX=2.5 StartY=0 StartZ=0 EndX=4.2 EndY=0 EndZ=0
    g2: LineSegment StartX=4.2 StartY=0 StartZ=0 EndX=4.2 EndY=2 EndZ=0
    g3: LineSegment StartX=4.2 StartY=2 StartZ=0 EndX=9.9 EndY=2 EndZ=0
    g4: LineSegment StartX=9.9 StartY=2 StartZ=0 EndX=9.9 EndY=4.4 EndZ=0
    g5: LineSegment StartX=9.9 StartY=4.4 StartZ=0 EndX=1.5 EndY=4.4 EndZ=0
    g6: LineSegment StartX=1.5 StartY=4.4 StartZ=0 EndX=1.5 EndY=3.4 EndZ=0
    g7: LineSegment StartX=1.5 StartY=3.4 StartZ=0 EndX=2.5 EndY=3.4 EndZ=0
  constraints (24):
    c: PointOnObject(g0,g-1)
    c: Vertical(g0)
    c: Coincident(g1,g0)
    c: PointOnObject(g1,g-1)
    c: Coincident(g2,g1)
    c: Vertical(g2)
    c: Coincident(g3,g2)
    c: Horizontal(g3)
    c: Coincident(g4,g3)
    c: Vertical(g4)
    c: Coincident(g5,g4)
    c: Horizontal(g5)
    c: Coincident(g6,g5)
    c: Coincident(g7,g6)
    c: Coincident(g7,g0)
    c: Horizontal(g7)
    c: Vertical(g6)
    c: DistanceY(g4,g4) = 2.4
    c: DistanceY(g2,g2) = 2
    c: DistanceX(g-1,g4) = 9.9
    c: DistanceX(g-1,g6) = 1.5
    c: DistanceY(g0,g0) = 3.4
    c: DistanceX(g-1,g0) = 2.5
    c: DistanceX(g1,g1) = 1.7
FEATURE [PartDesign::Revolution] Revolution001
  Angle = 360
  Angle2 = 60
  Axis = (0,2e-16,1)
  Base = (0,0,0)
  Placement = pos=(0,0,0) rot=(1,0,0;1.5708rad)
  Profile = -> Sketch048
  ReferenceAxis = -> Sketch048 [V_Axis]
  Reversed = true
  Suppressed = false
  Type = 0
FEATURE [Sketcher::SketchObject] Sketch049
  ArcFitTolerance = 0
  AttachmentSupport = -> [XY_Plane021]
  FullyConstrained = true
  MakeInternals = false
  MapMode = 5
  sketch-geometry (1):
    g0: Circle CenterX=-7 CenterY=0 CenterZ=0 NormalX=0 NormalY=0 NormalZ=1 AngleXU=0 Radius=1.2
  constraints (3):
    c: PointOnObject(g0,g-1)
    c: Diameter(g0) = 2.4
    c: DistanceX(g0,g-1) = 7
FEATURE [PartDesign::Pocket] Pocket025
  BaseFeature = -> Revolution001
  Direction = (0,0,-1)
  Length = 5
  Length2 = 5
  Midplane = true
  Placement = pos=(0,0,0) rot=(1,0,0;1.5708rad)
  Profile = -> Sketch049
  ReferenceAxis = -> Sketch049 [N_Axis]
  Suppressed = false
  Type = 1
FEATURE [PartDesign::PolarPattern] PolarPattern003
  Angle = 360
  Axis = -> Sketch049 [N_Axis]
  BaseFeature = -> Pocket025
  Mode = 0
  Occurrences = 4
  Offset = 120
  Originals = -> [Pocket025]
  Placement = pos=(0,0,0) rot=(1,0,0;1.5708rad)
  Suppressed = false
  TransformMode = 0
FEATURE [PartDesign::Body] Body014  label="Corps001"
  AllowCompound = false
  Group = -> [Sketch048,Revolution001,Sketch049,Pocket025,PolarPattern003]
  Origin = -> Origin021
  Placement = pos=(0,0,0.4) rot=(0,0,1;0rad)
  Tip = -> PolarPattern003
FEATURE [App::Part] Part007  label="servo_DS3218MG002"
  Group = -> [Part__Feature008002002006400,Part__Feature008002002006401,Part__Feature008002002006402,Body014,Screw004]
  Origin = -> Origin020
  Placement = pos=(45,-3.7e-15,41.5) rot=(0,0,1;0rad)
FEATURE [Sketcher::SketchObject] Sketch055
  ArcFitTolerance = 1e-06
  AttachmentSupport = -> [XY_Plane019]
  ExternalGeometry = -> [Pad015]
  FullyConstrained = true
  MakeInternals = false
  MapMode = 5
  Placement = pos=(0,0,0) rot=(0,1,0;3.14159rad)
  sketch-geometry (8):
    g0: LineSegment StartX=-6.575 StartY=4.575 StartZ=0 EndX=-6.575 EndY=-4.575 EndZ=0
    g1: LineSegment StartX=-6.575 StartY=-4.575 StartZ=0 EndX=0.075 EndY=-4.575 EndZ=0
    g2: LineSegment StartX=0.075 StartY=-4.575 StartZ=0 EndX=0.075 EndY=4.575 EndZ=0
    g3: LineSegment StartX=0.075 StartY=4.575 StartZ=0 EndX=-6.575 EndY=4.575 EndZ=0
    g4: LineSegment StartX=-18.425 StartY=-15.925 StartZ=0 EndX=-18.425 EndY=-34.075 EndZ=0
    g5: LineSegment StartX=-18.425 StartY=-34.075 StartZ=0 EndX=-6.425 EndY=-34.075 EndZ=0
    g6: LineSegment StartX=-6.425 StartY=-34.075 StartZ=0 EndX=-6.425 EndY=-15.925 EndZ=0
    g7: LineSegment StartX=-6.425 StartY=-15.925 StartZ=0 EndX=-18.425 EndY=-15.925 EndZ=0
  constraints (22):
    c: Coincident(g0,g1)
    c: Coincident(g1,g2)
    c: Coincident(g2,g3)
    c: Coincident(g3,g0)
    c: Vertical(g0)
    c: Vertical(g2)
    c: Horizontal(g1)
    c: Horizontal(g3)
    c: Coincident(g4,g5)
    c: Coincident(g5,g6)
    c: Coincident(g6,g7)
    c: Coincident(g7,g4)
    c: Vertical(g4)
    c: Vertical(g6)
    c: Horizontal(g5)
    c: Horizontal(g7)
    c: PointOnObject(g4,g-5)
    c: PointOnObject(g6,g-6)
    c: PointOnObject(g5,g-7)
    c: DistanceX(g7,g7) = 12
    c: Coincident(g0,g-3)
    c: Coincident(g1,g-4)
FEATURE [PartDesign::Pad] Pad023
  BaseFeature = -> Pad015
  Direction = (0,0,-1)
  Length = 5
  Length2 = 10
  Profile = -> Sketch055
  ReferenceAxis = -> Sketch055 [N_Axis]
  Reversed = true
  Suppressed = false
  Type = 0
FEATURE [Sketcher::SketchObject] Sketch056
  ArcFitTolerance = 1e-06
  AttachmentOffset = pos=(0,0,-0.25) rot=(0,0,1;0rad)
  AttachmentSupport = -> [YZ_Plane019]
  ExternalGeometry = -> [Pad023]
  FullyConstrained = true
  MakeInternals = false
  MapMode = 5
  Placement = pos=(-0.25,0,0) rot=(0.57735,0.57735,0.57735;2.0944rad)
  sketch-geometry (7):
    g0: LineSegment StartX=-8.575 StartY=27.5 StartZ=0 EndX=8.575 EndY=27.5 EndZ=0
    g1: LineSegment StartX=4.575 StartY=31.5 StartZ=0 EndX=4.575 EndY=34.5 EndZ=0
    g2: LineSegment StartX=-4.575 StartY=34.5 StartZ=0 EndX=-4.575 EndY=31.5 EndZ=0
    g3: ArcOfCircle CenterX=0 CenterY=34.5 CenterZ=0 NormalX=0 NormalY=0 NormalZ=1 AngleXU=0 Radius=4.575 StartAngle=0 EndAngle=3.14159
    g4: Circle CenterX=0 CenterY=34.5 CenterZ=0 NormalX=0 NormalY=0 NormalZ=1 AngleXU=0 Radius=1.75
    g5: ArcOfCircle CenterX=-8.575 CenterY=31.5 CenterZ=0 NormalX=0 NormalY=0 NormalZ=1 AngleXU=0 Radius=4 StartAngle=4.71239 EndAngle=6.28319
    g6: ArcOfCircle CenterX=8.575 CenterY=31.5 CenterZ=0 NormalX=0 NormalY=0 NormalZ=1 AngleXU=0 Radius=4 StartAngle=3.14159 EndAngle=4.71239
  constraints (17):
    c: Vertical(g1)
    c: Vertical(g2)
    c: PointOnObject(g3,g-2)
    c: DistanceY(g-1,g3) = 34.5
    c: Tangent(g3,g1) = -1.5708
    c: Coincident(g4,g3)
    c: Diameter(g4) = 3.5
    c: Tangent(g3,g2) = -1.5708
    c: Tangent(g2,g5) = 1.5708
    c: Tangent(g0,g5) = -1.5708
    c: Horizontal(g0,g-3)
    c: Vertical(g2,g-3)
    c: Horizontal(g0,g-3)
    c: Tangent(g6,g1) = 1.5708
    c: Tangent(g0,g6) = -1.5708
    c: Equal(g1,g2)
    c: Radius(g6) = 4
FEATURE [PartDesign::Pad] Pad024
  BaseFeature = -> Pad023
  Direction = (1,0,0)
  Length = 4
  Length2 = 10
  Profile = -> Sketch056
  ReferenceAxis = -> Sketch056 [N_Axis]
  Reversed = true
  Suppressed = false
  Type = 0
FEATURE [Sketcher::SketchObject] Sketch057
  ArcFitTolerance = 1e-06
  AttachmentSupport = -> [XY_Plane019]
  ExternalGeometry = -> [Pad024]
  FullyConstrained = true
  MakeInternals = false
  MapMode = 5
  sketch-geometry (14):
    g0: ArcOfCircle CenterX=34.5 CenterY=-16 CenterZ=0 NormalX=0 NormalY=0 NormalZ=1 AngleXU=0 Radius=3 StartAngle=1.5708 EndAngle=3.14159
    g1: ArcOfCircle CenterX=39 CenterY=-20 CenterZ=0 NormalX=0 NormalY=0 NormalZ=1 AngleXU=0 Radius=5 StartAngle=4.34942 EndAngle=6.76197
    g2: LineSegment StartX=31.5 StartY=-16 StartZ=0 EndX=31.5 EndY=-22.5 EndZ=0
    g3: LineSegment StartX=34.5 StartY=-13 StartZ=0 EndX=41 EndY=-13 EndZ=0
    g4: Circle CenterX=39 CenterY=-20 CenterZ=0 NormalX=0 NormalY=0 NormalZ=1 AngleXU=0 Radius=1.75
    g5: LineSegment StartX=31.5 StartY=-22.5 StartZ=0 EndX=37.2247 EndY=-24.6742 EndZ=0
    g6: LineSegment StartX=43.4378 StartY=-17.6965 StartZ=0 EndX=41 EndY=-13 EndZ=0
    g7: Circle CenterX=29.2 CenterY=20 CenterZ=0 NormalX=0 NormalY=0 NormalZ=1 AngleXU=0 Radius=1.75
    g8: LineSegment StartX=20.2 StartY=13 StartZ=0 EndX=38.2 EndY=13 EndZ=0
    g9: LineSegment StartX=34.2 StartY=17 StartZ=0 EndX=34.2 EndY=20 EndZ=0
    g10: LineSegment StartX=24.2 StartY=17 StartZ=0 EndX=24.2 EndY=20 EndZ=0
    g11: ArcOfCircle CenterX=29.2 CenterY=20 CenterZ=0 NormalX=0 NormalY=0 NormalZ=1 AngleXU=0 Radius=5 StartAngle=0 EndAngle=3.14159
    g12: ArcOfCircle CenterX=20.2 CenterY=17 CenterZ=0 NormalX=0 NormalY=0 NormalZ=1 AngleXU=0 Radius=4 StartAngle=4.71239 EndAngle=6.28319
    g13: ArcOfCircle CenterX=38.2 CenterY=17 CenterZ=0 NormalX=0 NormalY=0 NormalZ=1 AngleXU=0 Radius=4 StartAngle=3.14159 EndAngle=4.71239
  constraints (34):
    c: Coincident(g0,g-3)
    c: Coincident(g3,g0)
    c: Horizontal(g3)
    c: Vertical(g2)
    c: Tangent(g2,g0) = -1.5708
    c: Coincident(g0,g-3)
    c: Coincident(g4,g1)
    c: Diameter(g4) = 3.5
    c: Radius(g1) = 5
    c: Coincident(g2,g5)
    c: Tangent(g5,g1) = -1.5708
    c: Coincident(g6,g3)
    c: Tangent(g6,g1) = -1.5708
    c: Equal(g3,g2)
    c: DistanceX(g3,g3) = 6.5
    c: Horizontal(g8)
    c: Vertical(g9)
    c: Vertical(g10)
    c: PointOnObject(g8,g-4)
    c: Coincident(g7,g11)
    c: Tangent(g11,g9) = -1.5708
    c: Tangent(g11,g10) = 1.5708
    c: Tangent(g10,g12) = -1.5708
    c: Tangent(g8,g12) = -1.5708
    c: Tangent(g13,g9) = 1.5708
    c: Tangent(g13,g8) = -1.5708
    c: Diameter(g7) = 3.5
    c: Equal(g11,g1)
    c: Equal(g10,g9)
    c: Radius(g13) = 4
    c: DistanceY(g-1,g7) = 20
    c: DistanceX(g-1,g7) = 29.2
    c: DistanceY(g1,g-1) = 20
    c: DistanceX(g-1,g1) = 39
FEATURE [PartDesign::Pad] Pad025
  BaseFeature = -> Pad024
  Direction = (0,0,1)
  Length = 3
  Length2 = 10
  Profile = -> Sketch057
  ReferenceAxis = -> Sketch057 [N_Axis]
  Suppressed = false
  Type = 0
FEATURE [Sketcher::SketchObject] Sketch058
  ArcFitTolerance = 1e-06
  AttachmentOffset = pos=(15,9.6,25) rot=(0,0,1;0rad)
  AttachmentSupport = -> [XZ_Plane019]
  FullyConstrained = true
  MakeInternals = false
  MapMode = 5
  Placement = pos=(15,-25,9.6) rot=(1,0,0;1.5708rad)
  sketch-geometry (2):
    g0: ArcOfCircle CenterX=0 CenterY=0 CenterZ=0 NormalX=0 NormalY=0 NormalZ=1 AngleXU=0 Radius=2.25 StartAngle=1.99427 EndAngle=7.43051
    g1: ArcOfCircle CenterX=0 CenterY=1 CenterZ=0 NormalX=0 NormalY=0 NormalZ=1 AngleXU=0 Radius=1.4 StartAngle=0.849413 EndAngle=2.29218
  constraints (7):
    c: Coincident(g0,g-1)
    c: Diameter(g0) = 4.5
    c: Coincident(g1,g0)
    c: Coincident(g1,g0)
    c: PointOnObject(g1,g-2)
    c: DistanceY(g0,g1) = 1
    c: Radius(g1) = 1.4
FEATURE [PartDesign::Pocket] Pocket028
  BaseFeature = -> Pad025
  Direction = (0,1,-2e-16)
  Length = 27
  Length2 = 5
  Midplane = true
  Profile = -> Sketch058
  ReferenceAxis = -> Sketch058 [N_Axis]
  Suppressed = false
  Type = 0
FEATURE [Sketcher::SketchObject] Sketch059
  ArcFitTolerance = 1e-06
  AttachmentSupport = -> [Pocket028]
  ExternalGeometry = -> [Pocket028]
  FullyConstrained = true
  MakeInternals = false
  MapMode = 5
  Placement = pos=(0,0,27.5) rot=(0,0,1;0rad)
  sketch-geometry (2):
    g0: Circle CenterX=10.5 CenterY=6 CenterZ=0 NormalX=0 NormalY=0 NormalZ=1 AngleXU=0 Radius=2.1
    g1: Circle CenterX=10.5 CenterY=-6 CenterZ=0 NormalX=0 NormalY=0 NormalZ=1 AngleXU=0 Radius=2.1
  constraints (4):
    c: Coincident(g0,g-3)
    c: Coincident(g1,g-4)
    c: Equal(g0,g1)
    c: Diameter(g0) = 4.2
FEATURE [PartDesign::Pocket] Pocket029
  BaseFeature = -> Pocket028
  Direction = (0,0,-1)
  Length = 1.5
  Length2 = 5
  Profile = -> Sketch059
  ReferenceAxis = -> Sketch059 [N_Axis]
  Suppressed = false
  Type = 0
FEATURE [Sketcher::SketchObject] Sketch060
  ArcFitTolerance = 1e-06
  AttachmentSupport = -> [XZ_Plane023]
  FullyConstrained = true
  MakeInternals = false
  MapMode = 5
  Placement = pos=(0,0,0) rot=(0,0.707107,0.707107;3.14159rad)
  sketch-geometry (6):
    g0: ArcOfCircle CenterX=0 CenterY=0 CenterZ=0 NormalX=0 NormalY=0 NormalZ=1 AngleXU=0 Radius=5 StartAngle=3.14159 EndAngle=6.28319
    g1: ArcOfCircle CenterX=-1.246e-13 CenterY=21 CenterZ=0 NormalX=0 NormalY=0 NormalZ=1 AngleXU=0 Radius=5 StartAngle=-7.64e-14 EndAngle=3.14159
    g2: LineSegment StartX=-5 StartY=9.017e-13 StartZ=0 EndX=-5 EndY=21 EndZ=0
    g3: LineSegment StartX=5 StartY=6.3e-15 StartZ=0 EndX=5 EndY=21 EndZ=0
    g4: Circle CenterX=0 CenterY=0 CenterZ=0 NormalX=0 NormalY=0 NormalZ=1 AngleXU=0 Radius=2.25
    g5: Circle CenterX=-1.246e-13 CenterY=21 CenterZ=0 NormalX=0 NormalY=0 NormalZ=1 AngleXU=0 Radius=2.25
  constraints (13):
    c: Tangent(g0,g2) = 1.5708
    c: Tangent(g0,g3) = -1.5708
    c: Tangent(g1,g2) = 1.5708
    c: Tangent(g1,g3) = -1.5708
    c: Equal(g0,g1)
    c: Vertical(g3)
    c: Coincident(g0,g-1)
    c: DistanceY(g0,g1) = 21  'longueur_extention'
    c: Radius(g0) = 5
    c: Diameter(g4) = 4.5
    c: Coincident(g4,g0)
    c: Diameter(g5) = 4.5
    c: Coincident(g5,g1)
FEATURE [PartDesign::Pad] Pad026
  Direction = (0,1,-2e-16)
  Length = 5
  Length2 = 10
  Placement = pos=(0,0,0) rot=(1,0,0;1.5708rad)
  Profile = -> Sketch060
  ReferenceAxis = -> Sketch060 [N_Axis]
  Suppressed = false
  Type = 0
FEATURE [Sketcher::SketchObject] Sketch061
  ArcFitTolerance = 1e-06
  AttachmentSupport = -> [XZ_Plane023]
  ExternalGeometry = -> [Pad026]
  FullyConstrained = false
  MakeInternals = false
  MapMode = 5
  Placement = pos=(0,0,0) rot=(1,0,0;1.5708rad)
  sketch-geometry (6):
    g0: LineSegment StartX=-5 StartY=1 StartZ=0 EndX=-5 EndY=-1.6e-15 EndZ=0
    g1: LineSegment StartX=-4.89898 StartY=-1 StartZ=0 EndX=-2.01556 EndY=-1 EndZ=0
    g2: LineSegment StartX=-2.01556 StartY=1 StartZ=0 EndX=-5 EndY=1 EndZ=0
    g3: ArcOfCircle CenterX=0 CenterY=0 CenterZ=0 NormalX=0 NormalY=0 NormalZ=1 AngleXU=0 Radius=5 StartAngle=3.14159 EndAngle=3.34295
    g4: ArcOfCircle CenterX=0 CenterY=0 CenterZ=0 NormalX=0 NormalY=0 NormalZ=1 AngleXU=0 Radius=2.25 StartAngle=2.68104 EndAngle=3.60215
    g5: LineSegment [constr] StartX=-4.17111 StartY=1 StartZ=0 EndX=-4.17111 EndY=-1 EndZ=0
  constraints (16):
    c: Coincident(g2,g0)
    c: Vertical(g0)
    c: Horizontal(g1)
    c: Horizontal(g2)
    c: PointOnObject(g1,g-4)
    c: Coincident(g3,g-1)
    c: Coincident(g3,g-3)
    c: Coincident(g4,g3)
    c: Coincident(g4,g1)
    c: Coincident(g0,g3)
    c: Coincident(g2,g4)
    c: Coincident(g1,g3)
    c: PointOnObject(g5,g2)
    c: PointOnObject(g5,g1)
    c: Symmetric(g5,g5,g-1)
    c: DistanceY(g5,g5) = 2
FEATURE [PartDesign::Pad] Pad027
  BaseFeature = -> Pad026
  Direction = (0,-1,2e-16)
  Length = 2
  Length2 = 10
  Placement = pos=(0,0,0) rot=(1,0,0;1.5708rad)
  Profile = -> Sketch061
  ReferenceAxis = -> Sketch061 [N_Axis]
  Suppressed = false
  Type = 0
FEATURE [PartDesign::Mirrored] Mirrored004
  BaseFeature = -> Pad027
  MirrorPlane = -> Sketch061 [V_Axis]
  Originals = -> [Pad027]
  Placement = pos=(0,0,0) rot=(1,0,0;1.5708rad)
  Suppressed = false
  TransformMode = 0
FEATURE [PartDesign::Body] Body016  label="extention_verrin"
  AllowCompound = false
  Group = -> [Sketch060,Pad026,Sketch061,Pad027,Mirrored004]
  Origin = -> Origin023
  Placement = pos=(9,13,0) rot=(0,0,1;0rad)
  Tip = -> Mirrored004
FEATURE [PartDesign::Pad] Pad028
  BaseFeature = -> Pad017
  Direction = (1.6e-15,1,-7e-16)
  Length = 2
  Length2 = 10
  Placement = pos=(0,0,0) rot=(1,1,1;2.0944rad)
  Profile = -> Pad017 [Face17,Face23,Face38]
  Suppressed = false
  Type = 0
FEATURE [Sketcher::SketchObject] Sketch062
  ArcFitTolerance = 1e-06
  AttachmentOffset = pos=(0,5,0) rot=(0,0,1;0rad)
  AttachmentSupport = -> [Pad028]
  ExternalGeometry = -> [Pad028]
  FullyConstrained = true
  MakeInternals = false
  MapMode = 5
  Placement = pos=(5,13,0) rot=(0.57735,0.57735,0.57735;4.18879rad)
  sketch-geometry (4):
    g0: LineSegment StartX=-1.15 StartY=0 StartZ=0 EndX=1.15 EndY=0 EndZ=0
    g1: LineSegment StartX=1.15 StartY=0 StartZ=0 EndX=1.15 EndY=6.5 EndZ=0
    g2: LineSegment StartX=1.15 StartY=6.5 StartZ=0 EndX=-1.15 EndY=6.5 EndZ=0
    g3: LineSegment StartX=-1.15 StartY=6.5 StartZ=0 EndX=-1.15 EndY=0 EndZ=0
  constraints (11):
    c: Coincident(g0,g1)
    c: Coincident(g1,g2)
    c: Coincident(g2,g3)
    c: Coincident(g3,g0)
    c: Horizontal(g2)
    c: Vertical(g1)
    c: Vertical(g3)
    c: PointOnObject(g-4,g2)
    c: DistanceX(g2,g2) = 2.3
    c: Symmetric(g0,g0,g-2)
    c: PointOnObject(g-1,g0)
FEATURE [PartDesign::Pocket] Pocket030
  BaseFeature = -> Pad028
  Direction = (1e-16,-1,1.4e-15)
  Length = 2
  Length2 = 5
  Placement = pos=(0,0,0) rot=(1,1,1;2.0944rad)
  Profile = -> Sketch062
  ReferenceAxis = -> Sketch062 [N_Axis]
  Suppressed = false
  Type = 0
FEATURE [PartDesign::Mirrored] Mirrored005
  BaseFeature = -> Pocket030
  MirrorPlane = -> Sketch062 [H_Axis]
  Originals = -> [Pocket030]
  Placement = pos=(0,0,0) rot=(1,1,1;2.0944rad)
  Suppressed = false
  TransformMode = 0
FEATURE [PartDesign::Fillet] Fillet
  Base = -> Pocket029 [Edge169,Edge108]
  BaseFeature = -> Pocket029
  Radius = 3
  SupportTransform = false
  Suppressed = false
  UseAllEdges = false
FEATURE [PartDesign::Body] Body013  label="support_pince_planche_bas"
  AllowCompound = false
  Group = -> [Sketch042,Pad015,Sketch055,Pad023,Sketch056,Pad024,Sketch057,Pad025,Sketch058,Pocket028,Sketch059,Pocket029,Fillet]
  Origin = -> Origin019
  Tip = -> Fillet
FEATURE [Sketcher::SketchObject] Sketch063
  ArcFitTolerance = 1e-06
  AttachmentSupport = -> [XY_Plane024]
  FullyConstrained = true
  MakeInternals = false
  MapMode = 5
  sketch-geometry (11):
    g0: LineSegment StartX=-3.15 StartY=4.65 StartZ=0 EndX=-3.15 EndY=-4.65 EndZ=0
    g1: LineSegment StartX=-3.15 StartY=-4.65 StartZ=0 EndX=3.15 EndY=-4.65 EndZ=0
    g2: LineSegment StartX=3.15 StartY=-4.65 StartZ=0 EndX=3.15 EndY=4.65 EndZ=0
    g3: LineSegment StartX=3.15 StartY=4.65 StartZ=0 EndX=-3.15 EndY=4.65 EndZ=0
    g4: LineSegment StartX=-6.15 StartY=4.65 StartZ=0 EndX=-6.15 EndY=-4.65 EndZ=0
    g5: LineSegment StartX=-3.15 StartY=-7.65 StartZ=0 EndX=38.5 EndY=-7.65 EndZ=0
    g6: LineSegment StartX=38.5 StartY=-7.65 StartZ=0 EndX=38.5 EndY=7.65 EndZ=0
    g7: LineSegment StartX=38.5 StartY=7.65 StartZ=0 EndX=-3.15 EndY=7.65 EndZ=0
    g8: ArcOfCircle CenterX=-3.15 CenterY=4.65 CenterZ=0 NormalX=0 NormalY=0 NormalZ=1 AngleXU=0 Radius=3 StartAngle=1.5708 EndAngle=3.14159
    g9: ArcOfCircle CenterX=-3.15 CenterY=-4.65 CenterZ=0 NormalX=0 NormalY=0 NormalZ=1 AngleXU=0 Radius=3 StartAngle=3.14159 EndAngle=4.71239
    g10: GeomPoint [constr] X=-6.15 Y=7.65 Z=0
  constraints (27):
    c: Coincident(g0,g1)
    c: Coincident(g1,g2)
    c: Coincident(g2,g3)
    c: Coincident(g3,g0)
    c: Vertical(g0)
    c: Vertical(g2)
    c: Horizontal(g1)
    c: Horizontal(g3)
    c: Tangent(g4,g8) = -1.5708
    c: Tangent(g4,g9) = -1.5708
    c: Tangent(g5,g9) = -1.5708
    c: Tangent(g7,g8) = -1.5708
    c: Vertical(g4)
    c: Horizontal(g5)
    c: Horizontal(g7)
    c: Equal(g8,g9)
    c: PointOnObject(g10,g4)
    c: PointOnObject(g10,g7)
    c: Radius(g9) = 3
    c: Coincident(g6,g7)
    c: Coincident(g5,g6)
    c: Symmetric(g6,g5,g-1)
    c: Symmetric(g2,g0,g-1)
    c: DistanceY(g0,g0) = 9.3
    c: DistanceX(g3,g3) = 6.3
    c: Coincident(g0,g8)
    c: DistanceX(g-1,g6) = 38.5
FEATURE [PartDesign::Pad] Pad029
  Direction = (0,0,1)
  Length = 5
  Length2 = 10
  Profile = -> Sketch063
  ReferenceAxis = -> Sketch063 [N_Axis]
  Suppressed = false
  Type = 0
FEATURE [Sketcher::SketchObject] Sketch064
  ArcFitTolerance = 1e-06
  AttachmentSupport = -> [Pad029]
  ExternalGeometry = -> [Pad029]
  FullyConstrained = true
  MakeInternals = false
  MapMode = 5
  Placement = pos=(38.5,0,0) rot=(0.57735,0.57735,0.57735;2.0944rad)
  sketch-geometry (8):
    g0: Circle CenterX=0 CenterY=16 CenterZ=0 NormalX=0 NormalY=0 NormalZ=1 AngleXU=0 Radius=2.75
    g1: LineSegment StartX=-7.65 StartY=19 StartZ=0 EndX=-7.65 EndY=5 EndZ=0
    g2: LineSegment StartX=7.65 StartY=5 StartZ=0 EndX=7.65 EndY=19 EndZ=0
    g3: LineSegment StartX=4.65 StartY=22 StartZ=0 EndX=-4.65 EndY=22 EndZ=0
    g4: ArcOfCircle CenterX=-4.65 CenterY=19 CenterZ=0 NormalX=0 NormalY=0 NormalZ=1 AngleXU=0 Radius=3 StartAngle=1.5708 EndAngle=3.14159
    g5: ArcOfCircle CenterX=4.65 CenterY=19 CenterZ=0 NormalX=0 NormalY=0 NormalZ=1 AngleXU=0 Radius=3 StartAngle=-9e-16 EndAngle=1.5708
    g6: GeomPoint [constr] X=-7.65 Y=22 Z=0
    g7: LineSegment StartX=-7.65 StartY=5 StartZ=0 EndX=7.65 EndY=5 EndZ=0
  constraints (19):
    c: Diameter(g0) = 5.5
    c: PointOnObject(g0,g-2)
    c: Tangent(g1,g4) = -1.5708
    c: Tangent(g2,g5) = -1.5708
    c: Tangent(g3,g5) = -1.5708
    c: Tangent(g3,g4) = -1.5708
    c: Vertical(g1)
    c: Vertical(g2)
    c: Horizontal(g3)
    c: PointOnObject(g6,g1)
    c: PointOnObject(g6,g3)
    c: Coincident(g1,g-3)
    c: Coincident(g2,g-3)
    c: Equal(g5,g4)
    c: Radius(g4) = 3
    c: DistanceY(g2,g0) = 11
    c: Coincident(g7,g1)
    c: Coincident(g7,g2)
    c: DistanceY(g0,g3) = 6
FEATURE [PartDesign::Pad] Pad030
  BaseFeature = -> Pad029
  Direction = (1,0,0)
  Length = 3
  Length2 = 10
  Profile = -> Sketch064
  ReferenceAxis = -> Sketch064 [N_Axis]
  Reversed = true
  Suppressed = false
  Type = 0
FEATURE [PartDesign::Chamfer] Chamfer  label="Chamfer001"
  Angle = 45
  Base = -> Pad030 [Edge19]
  BaseFeature = -> Pad030
  ChamferType = 1
  FlipDirection = false
  Size = 15
  Size2 = 5
  SupportTransform = false
  Suppressed = false
  UseAllEdges = false
FEATURE [PartDesign::Body] Body017  label="support_pince_planche_haut"
  AllowCompound = false
  Group = -> [Sketch063,Pad029,Sketch064,Pad030,Chamfer]
  Origin = -> Origin024
  Placement = pos=(3,-2.563e-05,214) rot=(0,0,1;0rad)
  Tip = -> Chamfer
FEATURE [Sketcher::SketchObject] Sketch236
  ArcFitTolerance = 1e-06
  AttachmentSupport = -> [XZ_Plane278]
  FullyConstrained = true
  MakeInternals = false
  MapMode = 5
  Placement = pos=(0,0,0) rot=(1,0,0;1.5708rad)
  sketch-geometry (18):
    g0: LineSegment StartX=-4.5 StartY=0 StartZ=0 EndX=-4.5 EndY=-6 EndZ=0
    g1: LineSegment StartX=-4.5 StartY=-6 StartZ=0 EndX=12.3701 EndY=-6 EndZ=0
    g2: LineSegment StartX=17.2308 StartY=0.172017 StartZ=0 EndX=8.52786 EndY=36.2656 EndZ=0
    g3: LineSegment StartX=9.5 StartY=37.5 StartZ=0 EndX=21.5 EndY=37.5 EndZ=0
    g4: LineSegment StartX=21.5 StartY=37.5 StartZ=0 EndX=21.5 EndY=41.5 EndZ=0
    g5: LineSegment StartX=21.5 StartY=41.5 StartZ=0 EndX=8.47134 EndY=41.5 EndZ=0
    g6: LineSegment StartX=3.61064 StartY=35.328 StartZ=0 EndX=10.2 EndY=8 EndZ=0
    g7: LineSegment StartX=10.2 StartY=0 StartZ=0 EndX=-4.5 EndY=0 EndZ=0
    g8: ArcOfCircle CenterX=9.5 CenterY=36.5 CenterZ=0 NormalX=0 NormalY=0 NormalZ=1 AngleXU=0 Radius=1 StartAngle=1.5708 EndAngle=3.3782
    g9: GeomPoint [constr] X=8.23022 Y=37.5 Z=0
    g10: GeomPoint [constr] X=12.129 Y=0 Z=0
    g11: ArcOfCircle CenterX=12.3701 CenterY=-1 CenterZ=0 NormalX=0 NormalY=0 NormalZ=1 AngleXU=0 Radius=5 StartAngle=4.71239 EndAngle=6.51979
    g12: GeomPoint [constr] X=18.719 Y=-6 Z=0
    g13: GeomPoint X=15.5 Y=37.5 Z=0
    g14: LineSegment [constr] StartX=10.2 StartY=8 StartZ=0 EndX=15.0607 EndY=9.17202 EndZ=0
    g15: ArcOfCircle CenterX=8.47134 CenterY=36.5 CenterZ=0 NormalX=0 NormalY=0 NormalZ=1 AngleXU=0 Radius=5 StartAngle=1.5708 EndAngle=3.3782
    g16: GeomPoint [constr] X=2.12244 Y=41.5 Z=0
    g17: LineSegment StartX=10.2 StartY=0 StartZ=0 EndX=10.2 EndY=8 EndZ=0
  constraints (45):
    c: PointOnObject(g0,g-1)
    c: Vertical(g0)
    c: Coincident(g0,g1)
    c: Horizontal(g1)
    c: Horizontal(g3)
    c: Coincident(g3,g4)
    c: Vertical(g4)
    c: Coincident(g4,g5)
    c: Horizontal(g5)
    c: PointOnObject(g10,g-1)
    c: Coincident(g7,g0)
    c: DistanceY(g4,g4) = 4
    c: PointOnObject(g9,g3)
    c: PointOnObject(g9,g2)
    c: Tangent(g3,g8) = 1.5708
    c: Tangent(g2,g8) = 1.5708
    c: PointOnObject(g10,g6)
    c: PointOnObject(g10,g7)
    c: PointOnObject(g12,g1)
    c: PointOnObject(g12,g2)
    c: Tangent(g1,g11) = -1.5708
    c: Tangent(g2,g11) = -1.5708
    c: DistanceY(g0,g0) = 6
    c: DistanceX(g0,g-1) = 4.5
    c: Radius(g11) = 5
    c: Radius(g8) = 1
    c: DistanceX(g3,g3) = 12
    c: Symmetric(g3,g3,g13)
    c: DistanceX(g-1,g13) = 15.5
    c: DistanceY(g-1,g16) = 41.5
    c: Parallel(g2,g6)
    c: DistanceX(g-1,g7) = 10.2
    c: Coincident(g14,g6)
    c: PointOnObject(g14,g2)
    c: Perpendicular(g2,g14)
    c: Distance(g14,g14) = 5
    c: PointOnObject(g16,g5)
    c: PointOnObject(g16,g6)
    c: Tangent(g5,g15) = -1.5708
    c: Tangent(g6,g15) = -1.5708
    c: Radius(g15) = 5
    c: Coincident(g17,g7)
    c: Coincident(g17,g6)
    c: Vertical(g17)
    c: DistanceY(g17,g17) = 8
FEATURE [PartDesign::Pad] Pad114
  Direction = (0,-1,2e-16)
  Length = 13
  Length2 = 10
  Midplane = true
  Placement = pos=(0,0,0) rot=(1,0,0;1.5708rad)
  Profile = -> Sketch236
  ReferenceAxis = -> Sketch236 [N_Axis]
  Suppressed = false
  Type = 0
FEATURE [Sketcher::SketchObject] Sketch237
  ArcFitTolerance = 1e-06
  AttachmentSupport = -> [Pad114]
  ExternalGeometry = -> [Pad114]
  FullyConstrained = true
  MakeInternals = false
  MapMode = 5
  Placement = pos=(0,6.5,0) rot=(-1,0,0;1.5708rad)
  sketch-geometry (4):
    g0: LineSegment StartX=-4.5 StartY=0 StartZ=0 EndX=-4.5 EndY=-1.5 EndZ=0
    g1: LineSegment StartX=-4.5 StartY=-1.5 StartZ=0 EndX=12.5 EndY=-1.5 EndZ=0
    g2: LineSegment StartX=12.5 StartY=-1.5 StartZ=0 EndX=12.5 EndY=0 EndZ=0
    g3: LineSegment StartX=12.5 StartY=0 StartZ=0 EndX=-4.5 EndY=0 EndZ=0
  constraints (11):
    c: Coincident(g0,g1)
    c: Coincident(g1,g2)
    c: Coincident(g2,g3)
    c: Coincident(g3,g0)
    c: Vertical(g0)
    c: Vertical(g2)
    c: Horizontal(g1)
    c: Horizontal(g3)
    c: Coincident(g0,g-3)
    c: DistanceY(g0,g0) = 1.5
    c: DistanceX(g3,g3) = 17
FEATURE [PartDesign::Pad] Pad115
  BaseFeature = -> Pad114
  Direction = (0,1,2e-16)
  Length = 1.9
  Length2 = 10
  Placement = pos=(0,0,0) rot=(1,0,0;1.5708rad)
  Profile = -> Sketch237
  ReferenceAxis = -> Sketch237 [N_Axis]
  Refine = true
  Reversed = true
  Suppressed = false
  Type = 0
FEATURE [PartDesign::Mirrored] Mirrored010
  BaseFeature = -> Pad115
  MirrorPlane = -> XZ_Plane278
  Originals = -> [Pad115]
  Placement = pos=(0,0,0) rot=(1,0,0;1.5708rad)
  Refine = true
  Suppressed = false
  TransformMode = 0
FEATURE [Sketcher::SketchObject] Sketch235
  ArcFitTolerance = 1e-06
  AttachmentSupport = -> [Mirrored010]
  FullyConstrained = true
  MakeInternals = false
  MapMode = 5
  Placement = pos=(0,-2.6e-15,-6) rot=(1,0,0;3.14159rad)
  sketch-geometry (2):
    g0: Circle CenterX=0 CenterY=0 CenterZ=0 NormalX=0 NormalY=0 NormalZ=1 AngleXU=0 Radius=1.85
    g1: Circle CenterX=15.5 CenterY=0 CenterZ=0 NormalX=0 NormalY=0 NormalZ=1 AngleXU=0 Radius=2.75
  constraints (5):
    c: Diameter(g0) = 3.7
    c: Coincident(g0,g-1)
    c: Diameter(g1) = 5.5
    c: PointOnObject(g1,g-1)
    c: DistanceX(g-1,g1) = 15.5
FEATURE [PartDesign::Pocket] Pocket096
  BaseFeature = -> Mirrored010
  Direction = (0,0,1)
  Length = 5
  Length2 = 5
  Placement = pos=(0,0,0) rot=(1,0,0;1.5708rad)
  Profile = -> Sketch235
  ReferenceAxis = -> Sketch235 [N_Axis]
  Suppressed = false
  Type = 1
FEATURE [Sketcher::SketchObject] Sketch238
  ArcFitTolerance = 1e-06
  AttachmentSupport = -> [Pocket096]
  ExternalGeometry = -> [Pocket096]
  FullyConstrained = true
  MakeInternals = false
  MapMode = 5
  Placement = pos=(0,-2.6e-15,-6) rot=(1,0,0;3.14159rad)
  sketch-geometry (1):
    g0: Circle CenterX=0 CenterY=0 CenterZ=0 NormalX=0 NormalY=0 NormalZ=1 AngleXU=0 Radius=2.1
  constraints (2):
    c: Coincident(g0,g-1)
    c: Diameter(g0) = 4.2
FEATURE [PartDesign::Pocket] Pocket097
  BaseFeature = -> Pocket096
  Direction = (0,0,1)
  Length = 3
  Length2 = 5
  Placement = pos=(0,0,0) rot=(1,0,0;1.5708rad)
  Profile = -> Sketch238
  ReferenceAxis = -> Sketch238 [N_Axis]
  Suppressed = false
  Type = 0
FEATURE [Sketcher::SketchObject] Sketch239
  ArcFitTolerance = 1e-06
  AttachmentSupport = -> [Pocket097]
  FullyConstrained = true
  MakeInternals = false
  MapMode = 5
  Placement = pos=(0,-2.6e-15,-6) rot=(1,0,0;3.14159rad)
  sketch-geometry (1):
    g0: Circle CenterX=18 CenterY=0 CenterZ=0 NormalX=0 NormalY=0 NormalZ=1 AngleXU=0 Radius=5
  constraints (2):
    c: Diameter(g0) = 10
    c: Coincident(g0,g-3)
FEATURE [PartDesign::Pocket] Pocket098
  BaseFeature = -> Pocket097
  Direction = (0,0,1)
  Length = 25
  Length2 = 5
  Placement = pos=(0,0,0) rot=(1,0,0;1.5708rad)
  Profile = -> Sketch239
  ReferenceAxis = -> Sketch239 [N_Axis]
  Suppressed = false
  Type = 0
FEATURE [PartDesign::Fillet] Fillet001
  Base = -> Pocket098 [Edge63,Edge36,Edge37]
  BaseFeature = -> Pocket098
  Placement = pos=(0,0,0) rot=(1,0,0;1.5708rad)
  Radius = 0.81
  SupportTransform = false
  Suppressed = false
  UseAllEdges = false
FEATURE [PartDesign::Body] Body082  label="support_rail_haut"
  AllowCompound = false
  Group = -> [Sketch235,Sketch236,Pad114,Sketch237,Pad115,Mirrored010,Pocket096,Sketch238,Pocket097,Sketch239,Pocket098,Fillet001]
  Origin = -> Origin281
  Placement = pos=(2e-16,0,214.5) rot=(-0.707107,0,-0.707107;3.14159rad)
  Tip = -> Fillet001
FEATURE [Sketcher::SketchObject] Sketch240
  ArcFitTolerance = 1e-06
  AttachmentSupport = -> [XZ_Plane017]
  ExternalGeometry = -> [Mirrored005]
  FullyConstrained = true
  MakeInternals = false
  MapMode = 5
  Placement = pos=(0,0,0) rot=(1,0,0;1.5708rad)
  sketch-geometry (4):
    g0: ArcOfCircle CenterX=13.25 CenterY=20 CenterZ=0 NormalX=0 NormalY=0 NormalZ=1 AngleXU=0 Radius=11.25 StartAngle=3.14159 EndAngle=4.06889
    g1: LineSegment StartX=2 StartY=20 StartZ=0 EndX=0 EndY=20 EndZ=0
    g2: LineSegment StartX=0 StartY=20 StartZ=0 EndX=0 EndY=11 EndZ=0
    g3: LineSegment StartX=0 StartY=11 StartZ=0 EndX=6.5 EndY=11 EndZ=0
  constraints (11):
    c: Coincident(g0,g1)
    c: PointOnObject(g1,g-2)
    c: Coincident(g1,g2)
    c: Coincident(g2,g-3)
    c: Coincident(g2,g3)
    c: Coincident(g3,g-3)
    c: Horizontal(g1)
    c: Coincident(g0,g3)
    c: Horizontal(g0,g0)
    c: Distance(g1,g1) = 2
    c: DistanceY(g2,g2) = 9
FEATURE [PartDesign::Pad] Pad116
  BaseFeature = -> Mirrored005
  Direction = (0,-1,2e-16)
  Length = 22
  Length2 = 10
  Midplane = true
  Placement = pos=(0,0,0) rot=(1,1,1;2.0944rad)
  Profile = -> Sketch240
  ReferenceAxis = -> Sketch240 [N_Axis]
  Suppressed = false
  Type = 0
FEATURE [PartDesign::Body] Body012  label="jonction_rail_pince"
  AllowCompound = false
  Group = -> [Sketch036,Sketch037,Sketch038,Pad013,Pocket018,MultiTransform,Mirrored002,Mirrored003,Sketch040,AdditiveLoft,Sketch041,Pad014,Sketch043,Pad016,Sketch044,Pocket019,Sketch045,Pad018,Pad017,Pad028,Sketch062,Pocket030,Mirrored005,Sketch240,Pad116]
  Origin = -> Origin017
  Placement = pos=(4,0,0) rot=(0,0,1;0rad)
  Tip = -> Pad116
FEATURE [App::Part] Part
  Group = -> [Part__Feature008002002006397,Body012,Screw001,Body016]
  Origin = -> Origin016
  Placement = pos=(6,0,142.5) rot=(1,0,0;3.14159rad)
FEATURE [Part::FeaturePython] InvoluteGear001  label="InvoluteGear_11_77"  # WARN: FeaturePython — macro-defined, semantics opaque (R4)
  AttacherType = Attacher::AttachEngine3D
  addendum_diameter = 26
  angular_backlash = 0
  axle_hole = false
  axle_holesize = 10
  backlash = 0
  clearance = 0.25
  double_helix = false
  head = 0
  head_fillet = 0
  height = 5.5
  helix_angle = 0
  module = 1
  num_teeth = 24
  numpoints = 20
  offset_hole = false
  offset_holeoffset = 10
  offset_holesize = 10
  pitch_diameter = 24
  pressure_angle = 20
  properties_from_tool = false
  reversed_backlash = false
  root_diameter = 21.5
  root_fillet = 0
  shift = 0
  simple = false
  transverse_pitch = 3.14159
  traverse_module = 1
  undercut = false
  version = 1.3.0
  expr: angular_backlash = backlash / pitch_diameter * 360 ° / pi
FEATURE [PartDesign::FeatureBase] BaseFeature003
  BaseFeature = -> InvoluteGear001
  Suppressed = false
FEATURE [Part::FeaturePython] InvoluteRack001  label="InvoluteRack_11_77"  # WARN: FeaturePython — macro-defined, semantics opaque (R4)
  AttacherType = Attacher::AttachEngine3D
  add_endings = true
  clearance = 0.25
  double_helix = false
  head = 0
  head_fillet = 0
  height = 3
  helix_angle = 0
  module = 1
  num_teeth = 30
  pressure_angle = 20
  properties_from_tool = false
  root_fillet = 0
  simplified = false
  thickness = 9.5
  transverse_pitch = 3.14159
  version = 1.3.0
FEATURE [PartDesign::FeatureBase] BaseFeature002
  BaseFeature = -> InvoluteRack001
  Suppressed = false
FEATURE [App::FeaturePython] Joint001  label="Fixe001"  # Assembly joint (typed FeaturePython)
  Activated = true
  AngleMax = 0
  AngleMin = 0
  Detach1 = false
  Detach2 = false
  Distance = 0
  Distance2 = 0
  EnableAngleMax = false
  EnableAngleMin = false
  EnableLengthMax = false
  EnableLengthMin = false
  JointType = 0 (Fixed)
  LengthMax = 0
  LengthMin = 0
  Placement1 = pos=(4,36,20) rot=(0,0,1;0rad)
  Placement2 = pos=(29,41,0) rot=(0,0,1;0rad)
  Reference1 = -> Assembly002 [Body085.Edge130,Body085.Edge130]
  Reference2 = -> Assembly002 [Body087.Edge42,Body087.Edge42]
FEATURE [App::FeaturePython] Joint002  label="Fixe002"  # Assembly joint (typed FeaturePython)
  Activated = true
  AngleMax = 0
  AngleMin = 0
  Detach1 = false
  Detach2 = false
  Distance = 0
  Distance2 = 0
  EnableAngleMax = false
  EnableAngleMin = false
  EnableLengthMax = false
  EnableLengthMin = false
  JointType = 0 (Fixed)
  LengthMax = 0
  LengthMin = 0
  Placement1 = pos=(3.5,16.75,0) rot=(0,0,1;0rad)
  Placement2 = pos=(3.5,16.75,8) rot=(0,0,1;0rad)
  Reference1 = -> Assembly002 [Body083.Edge25,Body083.Edge25]
  Reference2 = -> Assembly002 [Body087.Edge56,Body087.Edge56]
FEATURE [App::FeaturePython] Joint003  label="Fixe003"  # Assembly joint (typed FeaturePython)
  Activated = true
  AngleMax = 0
  AngleMin = 0
  Detach1 = false
  Detach2 = false
  Distance = 0
  Distance2 = 0
  EnableAngleMax = false
  EnableAngleMin = false
  EnableLengthMax = false
  EnableLengthMin = false
  JointType = 0 (Fixed)
  LengthMax = 0
  LengthMin = 0
  Placement1 = pos=(-34.5,13.9,6) rot=(0.57735,0.57735,0.57735;4.18879rad)
  Placement2 = pos=(31,54.5,2) rot=(0,0,1;0rad)
  Reference1 = -> Assembly002 [Part002004.Part__Feature005.Edge1102,Part002004.Part__Feature005.Edge1102]
  Reference2 = -> Assembly002 [Body085.Edge46,Body085.Edge46]
FEATURE [App::FeaturePython] Joint004  label="Glissière"  # Assembly joint (typed FeaturePython)
  Activated = true
  AngleMax = 0
  AngleMin = 0
  Detach1 = false
  Detach2 = false
  Distance = 0
  Distance2 = 0
  EnableAngleMax = false
  EnableAngleMin = false
  EnableLengthMax = false
  EnableLengthMin = false
  JointType = 3 (Slider)
  LengthMax = 0
  LengthMin = 0
  Placement1 = pos=(0,2,4) rot=(0.707107,0,0.707107;3.14159rad)
  Placement2 = pos=(-10.75,48.0531,0) rot=(0.57735,0.57735,0.57735;4.18879rad)
  Reference1 = -> Assembly002 [Body087.Edge64,Body087.Vertex12]
  Reference2 = -> Assembly002 [Link004.Edge14,Link004.Edge14]
FEATURE [App::FeaturePython] Joint005  label="Pivot"  # Assembly joint (typed FeaturePython)
  Activated = true
  AngleMax = 0
  AngleMin = -71
  Detach1 = false
  Detach2 = false
  Distance = 0
  Distance2 = 0
  EnableAngleMax = false
  EnableAngleMin = false
  EnableLengthMax = false
  EnableLengthMin = false
  JointType = 1 (Revolute)
  LengthMax = 0
  LengthMin = 0
  Placement1 = pos=(0,0,5.5) rot=(0,0,1;0rad)
  Placement2 = pos=(0,0,0.897999) rot=(0,0,1;0rad)
  Reference1 = -> Assembly002 [Body086.Edge300,Body086.Edge300]
  Reference2 = -> Assembly002 [Part002004.Screw005.Edge22,Part002004.Screw005.Edge22]
FEATURE [App::FeaturePython] Joint006  label="Glissière001"  # Assembly joint (typed FeaturePython)
  Activated = true
  AngleMax = 0
  AngleMin = 0
  Detach1 = false
  Detach2 = false
  Distance = 0
  Distance2 = 0
  EnableAngleMax = false
  EnableAngleMin = false
  EnableLengthMax = false
  EnableLengthMin = false
  JointType = 3 (Slider)
  LengthMax = 0
  LengthMin = 0
  Placement1 = pos=(-10.75,48.0531,0) rot=(0.57735,0.57735,0.57735;4.18879rad)
  Placement2 = pos=(50,48,4) rot=(0.707107,0,0.707107;3.14159rad)
  Reference1 = -> Assembly002 [Body084.Edge14,Body084.Edge14]
  Reference2 = -> Assembly002 [Body087.Edge46,Body087.Edge46]
FEATURE [App::FeaturePython] Joint007  label="Fixe004"  # Assembly joint (typed FeaturePython)
  Activated = true
  AngleMax = 0
  AngleMin = 0
  Detach1 = false
  Detach2 = false
  Distance = 0
  Distance2 = 0
  EnableAngleMax = false
  EnableAngleMin = false
  EnableLengthMax = false
  EnableLengthMin = false
  JointType = 0 (Fixed)
  LengthMax = 0
  LengthMin = 0
  Offset2 = pos=(0,0,0) rot=(0,0,1;1.5708rad)
  Placement1 = pos=(9.25,92.677,40) rot=(0.707107,0,0.707107;3.14159rad)
  Placement2 = pos=(4.5,3.6e-15,3) rot=(-1,0,0;4.71239rad)
  Reference1 = -> Assembly002 [Body084.Edge263,Body084.Edge263]
  Reference2 = -> Assembly002 [Body088.Edge5,Body088.Edge5]
FEATURE [App::FeaturePython] Joint008  label="Fixe005"  # Assembly joint (typed FeaturePython)
  Activated = true
  AngleMax = 0
  AngleMin = 0
  Detach1 = false
  Detach2 = false
  Distance = 0
  Distance2 = 0
  EnableAngleMax = false
  EnableAngleMin = false
  EnableLengthMax = false
  EnableLengthMin = false
  JointType = 0 (Fixed)
  LengthMax = 0
  LengthMin = 0
  Offset2 = pos=(0,0,0) rot=(0,0,1;1.5708rad)
  Placement1 = pos=(4.5,0,3) rot=(-0.57735,-0.57735,0.57735;4.18879rad)
  Placement2 = pos=(9.25,92.677,40) rot=(0.57735,-0.57735,0.57735;4.18879rad)
  Reference1 = -> Assembly002 [Link005.Edge5,Link005.Edge5]
  Reference2 = -> Assembly002 [Link004.Edge263,Link004.Edge263]
FEATURE [App::FeaturePython] Joint009  label="Crémaillère"  # Assembly joint (typed FeaturePython)
  Activated = true
  AngleMax = 0
  AngleMin = 0
  Detach1 = false
  Detach2 = false
  Distance = 11.77
  Distance2 = 0
  EnableAngleMax = false
  EnableAngleMin = false
  EnableLengthMax = false
  EnableLengthMin = false
  JointType = 9 (RackPinion)
  LengthMax = 0
  LengthMin = 0
  Placement1 = pos=(-10.75,33.0531,3) rot=(0.57735,0.57735,0.57735;4.18879rad)
  Reference1 = -> Assembly002 [Body084.Edge8,Body084.Edge8]
  Reference2 = -> Assembly002 [Body086.Edge154,Body086.Edge154]
FEATURE [App::FeaturePython] Joint010  label="Crémaillère001"  # Assembly joint (typed FeaturePython)
  Activated = true
  AngleMax = 0
  AngleMin = 0
  Detach1 = false
  Detach2 = false
  Distance = 11.77
  Distance2 = 0
  EnableAngleMax = false
  EnableAngleMin = false
  EnableLengthMax = false
  EnableLengthMin = false
  JointType = 9 (RackPinion)
  LengthMax = 0
  LengthMin = 0
  Placement1 = pos=(-10.75,33.0531,3) rot=(0.57735,0.57735,0.57735;4.18879rad)
  Reference1 = -> Assembly002 [Link004.Edge8,Link004.Edge8]
  Reference2 = -> Assembly002 [Body086.Edge154,Body086.Edge154]
FEATURE [App::Link] Link004  label="pince_cremaillere_bras003"
  LinkPlacement = pos=(67.1598,7.75,24) rot=(0,0,1;1.5708rad)
  LinkedObject = -> Body084
  Placement = pos=(67.1598,7.75,24) rot=(0,0,1;1.5708rad)
FEATURE [App::Link] Link005  label="mousse003"
  LinkPlacement = pos=(-22.5171,17,59.5) rot=(0,-1,0;1.5708rad)
  LinkedObject = -> Body088
  Placement = pos=(-22.5171,17,59.5) rot=(0,-1,0;1.5708rad)
FEATURE [Part::Feature] Part__Feature003  label="Lever 25T002"
  Placement = pos=(0,0,0) rot=(-1,0,0;1.5708rad)
  shape: bbox 18.84 x 33.03 x 6.019 mm, 125 faces (baked)
FEATURE [Part::Feature] Part__Feature004  label="Axis Servo002"
  Placement = pos=(0,0,0) rot=(-1,0,0;1.5708rad)
  shape: bbox 5 x 5 x 8 mm, 5 faces (baked)
FEATURE [Part::Feature] Part__Feature005  label="Servo DS3218MG002"
  Placement = pos=(0,0,0) rot=(-1,0,0;1.5708rad)
  shape: bbox 55 x 20 x 41 mm, 772 faces (baked)
FEATURE [Part::FeaturePython] Screw005  label="M2x5-Vis001"  # WARN: FeaturePython — macro-defined, semantics opaque (R4)
  BaseObject = -> Body010 [Edge6]
  Diameter = 2
  Invert = true
  LeftHanded = false
  Length = 10
  LengthCustom = 5
  MatchOuter = false
  OffsetAngle = 0
  Placement = pos=(0,1e-15,4.8) rot=(0,0,1;0rad)
  Thread = false
  Type = 76
FEATURE [Sketcher::SketchObject] Sketch242
  ArcFitTolerance = 0
  AttachmentSupport = -> [XY_Plane281]
  FullyConstrained = true
  MakeInternals = false
  MapMode = 2
  sketch-geometry (31):
    g0: LineSegment StartX=0 StartY=50 StartZ=0 EndX=100 EndY=50 EndZ=0
    g1: LineSegment StartX=100 StartY=50 StartZ=0 EndX=100 EndY=48 EndZ=0
    g2: LineSegment StartX=100 StartY=0 StartZ=0 EndX=0 EndY=0 EndZ=0
    g3: LineSegment StartX=0 StartY=0 StartZ=0 EndX=0 EndY=2 EndZ=0
    g4: Circle CenterX=50 CenterY=25 CenterZ=0 NormalX=0 NormalY=0 NormalZ=1 AngleXU=0 Radius=14
    g5: LineSegment [constr] StartX=0 StartY=50 StartZ=0 EndX=100 EndY=0 EndZ=0
    g6: LineSegment [constr] StartX=0 StartY=0 StartZ=0 EndX=100 EndY=50 EndZ=0
    g7: LineSegment [constr] StartX=0 StartY=25 StartZ=0 EndX=100 EndY=25 EndZ=0
    g8: LineSegment [constr] StartX=50 StartY=50 StartZ=0 EndX=50 EndY=0 EndZ=0
    g9: LineSegment [constr] StartX=3.5 StartY=33.25 StartZ=0 EndX=96.5 EndY=33.25 EndZ=0
    g10: LineSegment [constr] StartX=96.5 StartY=33.25 StartZ=0 EndX=96.5 EndY=16.75 EndZ=0
    g11: LineSegment [constr] StartX=96.5 StartY=16.75 StartZ=0 EndX=3.5 EndY=16.75 EndZ=0
    g12: LineSegment [constr] StartX=3.5 StartY=16.75 StartZ=0 EndX=3.5 EndY=33.25 EndZ=0
    g13: Circle CenterX=96.5 CenterY=33.25 CenterZ=0 NormalX=0 NormalY=0 NormalZ=1 AngleXU=0 Radius=1.65
    g14: Circle CenterX=3.5 CenterY=33.25 CenterZ=0 NormalX=0 NormalY=0 NormalZ=1 AngleXU=0 Radius=1.65
    g15: Circle CenterX=3.5 CenterY=16.75 CenterZ=0 NormalX=0 NormalY=0 NormalZ=1 AngleXU=0 Radius=1.65
    g16: Circle CenterX=96.5 CenterY=16.75 CenterZ=0 NormalX=0 NormalY=0 NormalZ=1 AngleXU=0 Radius=1.65
    g17: LineSegment StartX=0 StartY=2 StartZ=0 EndX=30 EndY=2 EndZ=0
    g18: LineSegment StartX=30 StartY=2 StartZ=0 EndX=30 EndY=7.5 EndZ=0
    g19: LineSegment StartX=30 StartY=7.5 StartZ=0 EndX=2.5 EndY=7.5 EndZ=0
    g20: LineSegment StartX=0 StartY=10 StartZ=0 EndX=0 EndY=50 EndZ=0
    g21: LineSegment StartX=100 StartY=48 StartZ=0 EndX=67.5 EndY=48 EndZ=0
    g22: LineSegment StartX=67.5 StartY=48 StartZ=0 EndX=67.5 EndY=42.5 EndZ=0
    g23: LineSegment StartX=67.5 StartY=42.5 StartZ=0 EndX=97.5 EndY=42.5 EndZ=0
    g24: LineSegment StartX=100 StartY=40 StartZ=0 EndX=100 EndY=0 EndZ=0
    g25: ArcOfCircle [constr] CenterX=97.5 CenterY=40 CenterZ=0 NormalX=0 NormalY=0 NormalZ=1 AngleXU=0 Radius=2.5 StartAngle=0 EndAngle=1.5708
    g26: GeomPoint [constr] X=100 Y=42.5 Z=0
    g27: LineSegment StartX=100 StartY=40 StartZ=0 EndX=97.5 EndY=42.5 EndZ=0
    g28: ArcOfCircle [constr] CenterX=2.5 CenterY=10 CenterZ=0 NormalX=0 NormalY=0 NormalZ=1 AngleXU=0 Radius=2.5 StartAngle=3.14159 EndAngle=4.71239
    g29: GeomPoint [constr] X=0 Y=7.5 Z=0
    g30: LineSegment StartX=0 StartY=10 StartZ=0 EndX=2.5 EndY=7.5 EndZ=0
  constraints (78):
    c: Coincident(g0,g1)
    c: Coincident(g24,g2)
    c: Coincident(g2,g3)
    c: Coincident(g20,g0)
    c: Horizontal(g0)
    c: Horizontal(g2)
    c: Vertical(g1)
    c: Vertical(g3)
    c: Coincident(g2,g-1)
    c: Coincident(g5,g0)
    c: Coincident(g2,g6)
    c: Coincident(g0,g6)
    c: Coincident(g24,g5)
    c: PointOnObject(g4,g6)
    c: PointOnObject(g4,g5)
    c: Diameter(g4) = 28
    c: DistanceY(g3,g20) = 50
    c: DistanceX(g2,g2) = 100
    c: PointOnObject(g8,g0)
    c: PointOnObject(g7,g24)
    c: PointOnObject(g7,g20)
    c: PointOnObject(g8,g2)
    c: Symmetric(g0,g0,g8)
    c: Symmetric(g0,g2,g7)
    c: Coincident(g9,g10)
    c: Coincident(g10,g11)
    c: Coincident(g11,g12)
    c: Coincident(g12,g9)
    c: Horizontal(g11)
    c: Vertical(g12)
    c: Symmetric(g9,g10,g7)
    c: Symmetric(g9,g9,g8)
    c: Distance(g12) = 16.5
    c: DistanceX(g0,g9) = 3.5
    c: Coincident(g16,g10)
    c: Coincident(g13,g9)
    c: Coincident(g9,g14)
    c: Coincident(g11,g15)
    c: Equal(g14,g15)
    c: Equal(g14,g13)
    c: Equal(g14,g16)
    c: Diameter(g14) = 3.3
    c: Coincident(g17,g18)
    c: Coincident(g18,g19)
    c: Horizontal(g17)
    c: Horizontal(g19)
    c: Vertical(g18)
    c: Vertical(g20)
    c: DistanceX(g29,g19) = 30
    c: Coincident(g21,g22)
    c: Coincident(g22,g23)
    c: Horizontal(g21)
    c: Horizontal(g23)
    c: Vertical(g22)
    c: Vertical(g24)
    c: Equal(g18,g22)
    c: PointOnObject(g26,g23)
    c: PointOnObject(g26,g24)
    c: Tangent(g23,g25) = 1.5708
    c: Tangent(g24,g25) = 1.5708
    c: Coincident(g27,g23)
    c: Coincident(g27,g24)
    c: PointOnObject(g29,g20)
    c: PointOnObject(g29,g19)
    c: Tangent(g20,g28) = 1.5708
    c: Tangent(g19,g28) = 1.5708
    c: Coincident(g30,g20)
    c: Coincident(g30,g19)
    c: Equal(g1,g3)
    c: Equal(g23,g17)
    c: Coincident(g3,g17)
    c: DistanceY(g3,g3) = 2
    c: Coincident(g1,g21)
    c: Vertical(g1,g24)
    c: Vertical(g29,g3)
    c: DistanceY(g18,g18) = 5.5
    c: Radius(g28) = 2.5
    c: Equal(g25,g28)
FEATURE [PartDesign::Pad] Pad118
  AlongSketchNormal = false
  Direction = (0,0,1)
  Length = 4
  Length2 = 100
  Profile = -> Sketch242
  ReferenceAxis = -> Sketch242 [N_Axis]
  Suppressed = false
  Type = 0
FEATURE [Sketcher::SketchObject] Sketch243
  ArcFitTolerance = 1e-06
  AttachmentOffset = pos=(0,0,4) rot=(0,0,1;0rad)
  AttachmentSupport = -> [XY_Plane281]
  ExternalGeometry = -> [Pad118]
  FullyConstrained = true
  MakeInternals = false
  MapMode = 5
  Placement = pos=(0,0,4) rot=(0,0,1;0rad)
  sketch-geometry (4):
    g0: Circle CenterX=3.5 CenterY=33.25 CenterZ=0 NormalX=0 NormalY=0 NormalZ=1 AngleXU=0 Radius=3.25
    g1: Circle CenterX=3.5 CenterY=16.75 CenterZ=0 NormalX=0 NormalY=0 NormalZ=1 AngleXU=0 Radius=3.25
    g2: Circle CenterX=96.5 CenterY=33.25 CenterZ=0 NormalX=0 NormalY=0 NormalZ=1 AngleXU=0 Radius=3.25
    g3: Circle CenterX=96.5 CenterY=16.75 CenterZ=0 NormalX=0 NormalY=0 NormalZ=1 AngleXU=0 Radius=3.25
  constraints (10):
    c: Coincident(g0,g-3)
    c: Coincident(g1,g-4)
    c: Equal(g0,g1)
    c: Equal(g1,g2)
    c: Equal(g2,g3)
    c: Diameter(g0) = 6.5
    c: Horizontal(g3,g1)
    c: Horizontal(g2,g0)
    c: Vertical(g2,g3)
    c: DistanceX(g1,g3) = 93
FEATURE [PartDesign::Pocket] Pocket099
  BaseFeature = -> Pad118
  Direction = (0,0,-1)
  Length = 2
  Length2 = 5
  Profile = -> Sketch243
  ReferenceAxis = -> Sketch243 [N_Axis]
  Refine = true
  Suppressed = false
  Type = 0
FEATURE [PartDesign::Body] Body083  label="pince_capot001"
  AllowCompound = false
  Group = -> [Sketch242,Pad118,Sketch243,Pocket099]
  Origin = -> Origin284
  Placement = pos=(-25,-5,28) rot=(0,0,1;0rad)
  Tip = -> Pocket099
FEATURE [Sketcher::SketchObject] Sketch244
  ArcFitTolerance = 1e-06
  AttachmentSupport = -> [BaseFeature002]
  FullyConstrained = true
  MakeInternals = false
  MapMode = 5
  Placement = pos=(0,92.677,0) rot=(0,0.707107,0.707107;3.14159rad)
  sketch-geometry (4):
    g0: LineSegment StartX=-29.25 StartY=0 StartZ=0 EndX=10.75 EndY=0 EndZ=0
    g1: LineSegment StartX=10.75 StartY=0 StartZ=0 EndX=10.75 EndY=40 EndZ=0
    g2: LineSegment StartX=10.75 StartY=40 StartZ=0 EndX=-29.25 EndY=40 EndZ=0
    g3: LineSegment StartX=-29.25 StartY=40 StartZ=0 EndX=-29.25 EndY=0 EndZ=0
  constraints (12):
    c: Coincident(g0,g1)
    c: Coincident(g1,g2)
    c: Coincident(g2,g3)
    c: Coincident(g3,g0)
    c: Horizontal(g0)
    c: Horizontal(g2)
    c: Vertical(g1)
    c: Vertical(g3)
    c: DistanceY(g3,g3) = 40
    c: DistanceX(g2,g2) = 40
    c: PointOnObject(g0,g-1)
    c: DistanceX(g-1,g0) = 10.75
FEATURE [PartDesign::Pad] Pad119
  BaseFeature = -> BaseFeature002
  Direction = (0,1,-2e-16)
  Length = 5
  Length2 = 10
  Profile = -> Sketch244
  ReferenceAxis = -> Sketch244 [N_Axis]
  Refine = true
  Suppressed = false
  Type = 0
FEATURE [Sketcher::SketchObject] Sketch245
  ArcFitTolerance = 0
  AttachmentOffset = pos=(0,0,-2) rot=(0,0,1;0rad)
  AttachmentSupport = -> [XY_Plane283]
  FullyConstrained = true
  MakeInternals = false
  MapMode = 2
  Placement = pos=(0,0,-2) rot=(0,0,1;0rad)
  sketch-geometry (18):
    g0: LineSegment StartX=14.5 StartY=50 StartZ=0 EndX=35.5 EndY=50 EndZ=0
    g1: LineSegment StartX=35.5 StartY=50 StartZ=0 EndX=35.5 EndY=9 EndZ=0
    g2: LineSegment StartX=35.5 StartY=9 StartZ=0 EndX=14.5 EndY=9 EndZ=0
    g3: LineSegment StartX=14.5 StartY=9 StartZ=0 EndX=14.5 EndY=50 EndZ=0
    g4: LineSegment StartX=0 StartY=59 StartZ=0 EndX=50 EndY=59 EndZ=0
    g5: LineSegment StartX=50 StartY=59 StartZ=0 EndX=50 EndY=0 EndZ=0
    g6: LineSegment StartX=50 StartY=0 StartZ=0 EndX=0 EndY=0 EndZ=0
    g7: LineSegment StartX=0 StartY=0 StartZ=0 EndX=0 EndY=59 EndZ=0
    g8: Circle CenterX=19 CenterY=54.5 CenterZ=0 NormalX=0 NormalY=0 NormalZ=1 AngleXU=0 Radius=1.65
    g9: Circle CenterX=31 CenterY=54.5 CenterZ=0 NormalX=0 NormalY=0 NormalZ=1 AngleXU=0 Radius=1.65
    g10: Circle CenterX=19 CenterY=4.5 CenterZ=0 NormalX=0 NormalY=0 NormalZ=1 AngleXU=0 Radius=1.65
    g11: Circle CenterX=31 CenterY=4.5 CenterZ=0 NormalX=0 NormalY=0 NormalZ=1 AngleXU=0 Radius=1.65
    g12: LineSegment [constr] StartX=19 StartY=54.5 StartZ=0 EndX=31 EndY=54.5 EndZ=0
    g13: LineSegment [constr] StartX=31 StartY=54.5 StartZ=0 EndX=31 EndY=4.5 EndZ=0
    g14: LineSegment [constr] StartX=31 StartY=4.5 StartZ=0 EndX=19 EndY=4.5 EndZ=0
    g15: LineSegment [constr] StartX=19 StartY=4.5 StartZ=0 EndX=19 EndY=54.5 EndZ=0
    g16: LineSegment [constr] StartX=14.5 StartY=29.5 StartZ=0 EndX=35.5 EndY=29.5 EndZ=0
    g17: LineSegment [constr] StartX=25 StartY=50 StartZ=0 EndX=25 EndY=9 EndZ=0
  constraints (46):
    c: Coincident(g0,g1)
    c: Coincident(g1,g2)
    c: Coincident(g2,g3)
    c: Coincident(g3,g0)
    c: Horizontal(g0)
    c: Horizontal(g2)
    c: Vertical(g1)
    c: Vertical(g3)
    c: Coincident(g4,g5)
    c: Coincident(g5,g6)
    c: Coincident(g6,g7)
    c: Coincident(g7,g4)
    c: Horizontal(g6)
    c: Vertical(g5)
    c: Coincident(g12,g13)
    c: Coincident(g13,g14)
    c: Coincident(g14,g15)
    c: Coincident(g15,g12)
    c: Horizontal(g14)
    c: Vertical(g15)
    c: Coincident(g10,g14)
    c: Coincident(g11,g13)
    c: Coincident(g8,g12)
    c: Coincident(g9,g12)
    c: PointOnObject(g17,g0)
    c: PointOnObject(g17,g2)
    c: PointOnObject(g16,g3)
    c: PointOnObject(g16,g1)
    c: Symmetric(g0,g0,g17)
    c: Symmetric(g2,g0,g16)
    c: Symmetric(g9,g8,g17)
    c: DistanceX(g2,g2) = 21
    c: DistanceY(g3,g3) = 41
    c: DistanceX(g14,g14) = 12
    c: DistanceY(g13,g13) = 50
    c: Equal(g9,g8)
    c: Equal(g9,g11)
    c: Equal(g9,g10)
    c: Diameter(g9) = 3.3
    c: Symmetric(g9,g11,g16)
    c: Coincident(g-1,g6)
    c: Symmetric(g4,g4,g17)
    c: DistanceX(g6,g2) = 14.5
    c: Vertical(g7)
    c: DistanceY(g5,g5) = 59
    c: DistanceY(g-1,g2) = 9
FEATURE [PartDesign::Pad] Pad120
  AlongSketchNormal = false
  Direction = (0,0,1)
  Length = 4
  Length2 = 100
  Profile = -> Sketch245
  ReferenceAxis = -> Sketch245 [N_Axis]
  Suppressed = false
  Type = 0
FEATURE [Sketcher::SketchObject] Sketch246
  ArcFitTolerance = 0
  AttachmentSupport = -> [Pad120]
  ExternalGeometry = -> [Pad120]
  FullyConstrained = true
  MakeInternals = false
  MapMode = 5
  Placement = pos=(0,0,2) rot=(0,0,1;0rad)
  sketch-geometry (10):
    g0: LineSegment StartX=0 StartY=40 StartZ=0 EndX=8 EndY=40 EndZ=0
    g1: LineSegment StartX=8 StartY=40 StartZ=0 EndX=8 EndY=0 EndZ=0
    g2: LineSegment StartX=8 StartY=0 StartZ=0 EndX=0 EndY=0 EndZ=0
    g3: LineSegment StartX=0 StartY=0 StartZ=0 EndX=0 EndY=40 EndZ=0
    g4: LineSegment StartX=42 StartY=40 StartZ=0 EndX=50 EndY=40 EndZ=0
    g5: LineSegment StartX=50 StartY=40 StartZ=0 EndX=50 EndY=0 EndZ=0
    g6: LineSegment StartX=50 StartY=0 StartZ=0 EndX=42 EndY=0 EndZ=0
    g7: LineSegment StartX=42 StartY=0 StartZ=0 EndX=42 EndY=40 EndZ=0
    g8: LineSegment [constr] StartX=25 StartY=59 StartZ=0 EndX=25 EndY=0 EndZ=0
    g9: LineSegment [constr] StartX=0 StartY=20 StartZ=0 EndX=50 EndY=20 EndZ=0
  constraints (28):
    c: Coincident(g0,g1)
    c: Coincident(g1,g2)
    c: Coincident(g2,g3)
    c: Coincident(g3,g0)
    c: Horizontal(g0)
    c: Horizontal(g2)
    c: Vertical(g3)
    c: Coincident(g4,g5)
    c: Coincident(g5,g6)
    c: Coincident(g6,g7)
    c: Coincident(g7,g4)
    c: Horizontal(g4)
    c: Horizontal(g6)
    c: Vertical(g5)
    c: PointOnObject(g4,g-4)
    c: PointOnObject(g8,g-5)
    c: PointOnObject(g8,g-6)
    c: Symmetric(g-5,g-5,g8)
    c: Symmetric(g0,g4,g8)
    c: DistanceX(g0,g0) = 8
    c: Vertical(g1)
    c: PointOnObject(g9,g3)
    c: PointOnObject(g9,g5)
    c: Symmetric(g0,g1,g9)
    c: Vertical(g7)
    c: PointOnObject(g5,g-1)
    c: DistanceY(g3,g3) = 40
    c: Coincident(g2,g-1)
FEATURE [PartDesign::Pad] Pad121
  AlongSketchNormal = false
  BaseFeature = -> Pad120
  Direction = (0,0,1)
  Length = 18
  Length2 = 100
  Profile = -> Sketch246
  Suppressed = false
  Type = 0
FEATURE [Sketcher::SketchObject] Sketch247
  ArcFitTolerance = 0
  AttachmentSupport = -> [Pad121]
  ExternalGeometry = -> [Pad121]
  FullyConstrained = true
  MakeInternals = false
  MapMode = 5
  Placement = pos=(0,0,20) rot=(0,0,1;0rad)
  sketch-geometry (7):
    g0: LineSegment [constr] StartX=25 StartY=40 StartZ=0 EndX=25 EndY=0 EndZ=0
    g1: LineSegment [constr] StartX=0 StartY=20 StartZ=0 EndX=50 EndY=20 EndZ=0
    g2: Circle CenterX=4 CenterY=36 CenterZ=0 NormalX=0 NormalY=0 NormalZ=1 AngleXU=0 Radius=1.75
    g3: Circle CenterX=46 CenterY=36 CenterZ=0 NormalX=0 NormalY=0 NormalZ=1 AngleXU=0 Radius=1.75
    g4: Circle CenterX=4 CenterY=4 CenterZ=0 NormalX=0 NormalY=0 NormalZ=1 AngleXU=0 Radius=1.75
    g5: Circle CenterX=46 CenterY=4 CenterZ=0 NormalX=0 NormalY=0 NormalZ=1 AngleXU=0 Radius=1.75
    g6: LineSegment [constr] StartX=4 StartY=36 StartZ=0 EndX=4 EndY=4 EndZ=0
  constraints (17):
    c: PointOnObject(g0,g-4)
    c: PointOnObject(g0,g-5)
    c: PointOnObject(g1,g-7)
    c: PointOnObject(g1,g-8)
    c: Symmetric(g-3,g-4,g0)
    c: Symmetric(g-5,g-4,g1)
    c: Symmetric(g4,g2,g1)
    c: Symmetric(g3,g2,g0)
    c: Symmetric(g5,g3,g1)
    c: Equal(g2,g4)
    c: Equal(g2,g3)
    c: Equal(g2,g5)
    c: Radius(g2) = 1.75
    c: Coincident(g6,g4)
    c: Coincident(g6,g2)
    c: Symmetric(g-7,g-5,g6)
    c: DistanceY(g-5,g4) = 4
FEATURE [PartDesign::Pocket] Pocket100
  BaseFeature = -> Pad121
  Direction = (0,0,-1)
  Length = 5
  Length2 = 100
  Profile = -> Sketch247
  Suppressed = false
  Type = 1
FEATURE [Sketcher::SketchObject] Sketch248
  ArcFitTolerance = 0
  AttachmentSupport = -> [Pocket100]
  ExternalGeometry = -> [Pocket100]
  FullyConstrained = true
  MakeInternals = false
  MapMode = 5
  Placement = pos=(50,0,0) rot=(0.57735,0.57735,0.57735;2.0944rad)
  sketch-geometry (7):
    g0: LineSegment [constr] StartX=0 StartY=20 StartZ=0 EndX=40 EndY=0 EndZ=0
    g1: LineSegment [constr] StartX=0 StartY=0 StartZ=0 EndX=40 EndY=20 EndZ=0
    g2: Circle CenterX=12 CenterY=17 CenterZ=0 NormalX=0 NormalY=0 NormalZ=1 AngleXU=0 Radius=1.75
    g3: Circle CenterX=12 CenterY=3 CenterZ=0 NormalX=0 NormalY=0 NormalZ=1 AngleXU=0 Radius=1.75
    g4: Circle CenterX=28 CenterY=3 CenterZ=0 NormalX=0 NormalY=0 NormalZ=1 AngleXU=0 Radius=1.75
    g5: Circle CenterX=28 CenterY=17 CenterZ=0 NormalX=0 NormalY=0 NormalZ=1 AngleXU=0 Radius=1.75
    g6: GeomPoint X=20 Y=10 Z=0
  constraints (19):
    c: Equal(g3,g2)
    c: Equal(g3,g5)
    c: Equal(g3,g4)
    c: Coincident(g0,g-5)
    c: Coincident(g1,g-4)
    c: DistanceX(g-3,g-3) = 40
    c: Horizontal(g2,g5)
    c: Horizontal(g3,g4)
    c: Diameter(g3) = 3.5
    c: Vertical(g3,g2)
    c: Vertical(g5,g4)
    c: PointOnObject(g6,g0)
    c: PointOnObject(g6,g1)
    c: DistanceX(g2,g6) = 8
    c: DistanceY(g6,g2) = 7
    c: Symmetric(g2,g4,g6)
    c: Coincident(g1,g-1)
    c: PointOnObject(g0,g-1)
    c: Vertical(g-4,g0)
FEATURE [PartDesign::Pocket] Pocket101
  BaseFeature = -> Pocket100
  Direction = (-1,0,0)
  Length = 5
  Length2 = 100
  Profile = -> Sketch248
  ReferenceAxis = -> Sketch248 [N_Axis]
  Suppressed = false
  Type = 1
FEATURE [Sketcher::SketchObject] Sketch249
  ArcFitTolerance = 1e-06
  AttachmentSupport = -> [Pocket101]
  ExternalGeometry = -> [Pocket101]
  FullyConstrained = true
  MakeInternals = false
  MapMode = 5
  Placement = pos=(50,0,0) rot=(0.57735,0.57735,0.57735;2.0944rad)
  sketch-geometry (4):
    g0: Circle CenterX=12 CenterY=17 CenterZ=0 NormalX=0 NormalY=0 NormalZ=1 AngleXU=0 Radius=2.125
    g1: Circle CenterX=28 CenterY=17 CenterZ=0 NormalX=0 NormalY=0 NormalZ=1 AngleXU=0 Radius=2.125
    g2: Circle CenterX=28 CenterY=3 CenterZ=0 NormalX=0 NormalY=0 NormalZ=1 AngleXU=0 Radius=2.125
    g3: Circle CenterX=12 CenterY=3 CenterZ=0 NormalX=0 NormalY=0 NormalZ=1 AngleXU=0 Radius=2.125
  constraints (8):
    c: Equal(g0,g1)
    c: Equal(g1,g3)
    c: Equal(g3,g2)
    c: Diameter(g0) = 4.25
    c: Coincident(g0,g-3)
    c: Coincident(g-4,g1)
    c: Coincident(g-5,g2)
    c: Coincident(g-6,g3)
FEATURE [PartDesign::Pocket] Pocket102
  BaseFeature = -> Pocket101
  Direction = (-1,0,0)
  Length = 1.5
  Length2 = 5
  Profile = -> Sketch249
  ReferenceAxis = -> Sketch249 [N_Axis]
  Refine = true
  Suppressed = false
  Type = 0
FEATURE [Sketcher::SketchObject] Sketch250
  ArcFitTolerance = 1e-06
  AttachmentSupport = -> [Pocket102]
  ExternalGeometry = -> [Pocket102]
  FullyConstrained = true
  MakeInternals = false
  MapMode = 5
  Placement = pos=(0,0,0) rot=(0.57735,-0.57735,-0.57735;2.0944rad)
  sketch-geometry (4):
    g0: Circle CenterX=-28 CenterY=17 CenterZ=0 NormalX=0 NormalY=0 NormalZ=1 AngleXU=0 Radius=2.1
    g1: Circle CenterX=-12 CenterY=17 CenterZ=0 NormalX=0 NormalY=0 NormalZ=1 AngleXU=0 Radius=2.1
    g2: Circle CenterX=-12 CenterY=3 CenterZ=0 NormalX=0 NormalY=0 NormalZ=1 AngleXU=0 Radius=2.1
    g3: Circle CenterX=-28 CenterY=3 CenterZ=0 NormalX=0 NormalY=0 NormalZ=1 AngleXU=0 Radius=2.1
  constraints (8):
    c: Equal(g0,g1)
    c: Equal(g1,g3)
    c: Equal(g3,g2)
    c: Diameter(g0) = 4.2
    c: Coincident(g0,g-3)
    c: Coincident(g-4,g1)
    c: Coincident(g-5,g2)
    c: Coincident(g3,g-6)
FEATURE [PartDesign::Pocket] Pocket103
  BaseFeature = -> Pocket102
  Direction = (1,0,0)
  Length = 1.5
  Length2 = 5
  Profile = -> Sketch250
  ReferenceAxis = -> Sketch250 [N_Axis]
  Refine = true
  Suppressed = false
  Type = 0
FEATURE [Sketcher::SketchObject] Sketch251
  ArcFitTolerance = 1e-06
  AttachmentSupport = -> [Pocket103]
  ExternalGeometry = -> [Pocket103]
  FullyConstrained = true
  MakeInternals = false
  MapMode = 5
  Placement = pos=(0,0,20) rot=(0,0,1;0rad)
  sketch-geometry (4):
    g0: Circle CenterX=4 CenterY=36 CenterZ=0 NormalX=0 NormalY=0 NormalZ=1 AngleXU=0 Radius=2.1
    g1: Circle CenterX=46 CenterY=36 CenterZ=0 NormalX=0 NormalY=0 NormalZ=1 AngleXU=0 Radius=2.1
    g2: Circle CenterX=4 CenterY=4 CenterZ=0 NormalX=0 NormalY=0 NormalZ=1 AngleXU=0 Radius=2.1
    g3: Circle CenterX=46 CenterY=4 CenterZ=0 NormalX=0 NormalY=0 NormalZ=1 AngleXU=0 Radius=2.1
  constraints (8):
    c: Coincident(g0,g-3)
    c: Coincident(g1,g-6)
    c: Coincident(g2,g-4)
    c: Coincident(g3,g-5)
    c: Equal(g0,g2)
    c: Equal(g2,g1)
    c: Equal(g1,g3)
    c: Diameter(g0) = 4.2
FEATURE [PartDesign::Pocket] Pocket104
  BaseFeature = -> Pocket103
  Direction = (0,0,-1)
  Length = 1.5
  Length2 = 5
  Profile = -> Sketch251
  ReferenceAxis = -> Sketch251 [N_Axis]
  Refine = true
  Suppressed = false
  Type = 0
FEATURE [Sketcher::SketchObject] Sketch252
  ArcFitTolerance = 1e-06
  AttachmentSupport = -> [Pocket104]
  ExternalGeometry = -> [Pocket104]
  FullyConstrained = true
  MakeInternals = false
  MapMode = 5
  Placement = pos=(0,0,-2) rot=(1,0,0;3.14159rad)
  sketch-geometry (4):
    g0: Circle CenterX=4 CenterY=-4 CenterZ=0 NormalX=0 NormalY=0 NormalZ=1 AngleXU=0 Radius=2.1
    g1: Circle CenterX=46 CenterY=-4 CenterZ=0 NormalX=0 NormalY=0 NormalZ=1 AngleXU=0 Radius=2.1
    g2: Circle CenterX=46 CenterY=-36 CenterZ=0 NormalX=0 NormalY=0 NormalZ=1 AngleXU=0 Radius=2.1
    g3: Circle CenterX=4 CenterY=-36 CenterZ=0 NormalX=0 NormalY=0 NormalZ=1 AngleXU=0 Radius=2.1
  constraints (8):
    c: Coincident(g0,g-3)
    c: Coincident(g1,g-5)
    c: Coincident(g2,g-6)
    c: Coincident(g3,g-4)
    c: Equal(g0,g1)
    c: Equal(g1,g2)
    c: Equal(g2,g3)
    c: Diameter(g0) = 4.2
FEATURE [PartDesign::Pocket] Pocket105
  BaseFeature = -> Pocket104
  Direction = (0,0,1)
  Length = 1.5
  Length2 = 5
  Profile = -> Sketch252
  ReferenceAxis = -> Sketch252 [N_Axis]
  Refine = true
  Suppressed = false
  Type = 0
FEATURE [PartDesign::Body] Body085  label="pince_support_servo001"
  AllowCompound = false
  Group = -> [Sketch245,Pad120,Sketch246,Pad121,Sketch247,Pocket100,Sketch248,Pocket101,Sketch249,Pocket102,Sketch250,Pocket103,Sketch251,Pocket104,Sketch252,Pocket105]
  Origin = -> Origin286
  Tip = -> Pocket105
FEATURE [App::FeaturePython] GroundedJoint001  # Assembly grounded joint (typed FeaturePython)
  ObjectToGround = -> Body085
FEATURE [Assembly::JointGroup] Joints002
  Group = -> [GroundedJoint001,Joint001,Joint002,Joint003,Joint004,Joint005,Joint006,Joint007,Joint008,Joint009,Joint010]
FEATURE [Sketcher::SketchObject] Sketch253
  ArcFitTolerance = 0
  FullyConstrained = true
  MakeInternals = false
  MapMode = 5
  Placement = pos=(0,0,5.5) rot=(0,0,1;0rad)
  sketch-geometry (8):
    g0: Circle [constr] CenterX=0 CenterY=0 CenterZ=0 NormalX=0 NormalY=0 NormalZ=1 AngleXU=0 Radius=7
    g1: Circle CenterX=0 CenterY=7 CenterZ=0 NormalX=0 NormalY=0 NormalZ=1 AngleXU=0 Radius=1.65
    g2: Circle CenterX=-7 CenterY=0 CenterZ=0 NormalX=0 NormalY=0 NormalZ=1 AngleXU=0 Radius=1.65
    g3: Circle CenterX=7 CenterY=0 CenterZ=0 NormalX=0 NormalY=0 NormalZ=1 AngleXU=0 Radius=1.65
    g4: Circle CenterX=0 CenterY=-7 CenterZ=0 NormalX=0 NormalY=0 NormalZ=1 AngleXU=0 Radius=1.65
    g5: Circle CenterX=0 CenterY=0 CenterZ=0 NormalX=0 NormalY=0 NormalZ=1 AngleXU=0 Radius=3
    g6: LineSegment [constr] StartX=-7 StartY=0 StartZ=0 EndX=7 EndY=0 EndZ=0
    g7: LineSegment [constr] StartX=0 StartY=7 StartZ=0 EndX=0 EndY=-7 EndZ=0
  constraints (20):
    c: Coincident(g5,g0)
    c: Coincident(g5,g-1)
    c: PointOnObject(g2,g0)
    c: PointOnObject(g1,g0)
    c: PointOnObject(g3,g0)
    c: PointOnObject(g4,g0)
    c: Coincident(g2,g6)
    c: Coincident(g1,g7)
    c: Coincident(g6,g3)
    c: Coincident(g7,g4)
    c: PointOnObject(g5,g7)
    c: PointOnObject(g5,g6)
    c: Perpendicular(g7,g6)
    c: Equal(g1,g3)
    c: Equal(g1,g2)
    c: Equal(g1,g4)
    c: Diameter(g1) = 3.3
    c: Diameter(g5) = 6
    c: Diameter(g0) = 14
    c: PointOnObject(g2,g-1)
FEATURE [PartDesign::Pocket] Pocket106
  BaseFeature = -> BaseFeature003
  Direction = (0,0,-1)
  Length = 5
  Length2 = 100
  Profile = -> Sketch253
  Suppressed = false
  Type = 1
FEATURE [Sketcher::SketchObject] Sketch254
  ArcFitTolerance = 0
  AttachmentSupport = -> [Pocket106]
  ExternalGeometry = -> [Pocket106]
  FullyConstrained = true
  MakeInternals = false
  MapMode = 5
  Placement = pos=(0,0,0) rot=(1,0,0;3.14159rad)
  sketch-geometry (4):
    g0: Circle CenterX=0 CenterY=-7 CenterZ=0 NormalX=0 NormalY=0 NormalZ=1 AngleXU=0 Radius=3.25
    g1: Circle CenterX=-7 CenterY=0 CenterZ=0 NormalX=0 NormalY=0 NormalZ=1 AngleXU=0 Radius=3.25
    g2: Circle CenterX=7 CenterY=0 CenterZ=0 NormalX=0 NormalY=0 NormalZ=1 AngleXU=0 Radius=3.25
    g3: Circle CenterX=0 CenterY=7 CenterZ=0 NormalX=0 NormalY=0 NormalZ=1 AngleXU=0 Radius=3.25
  constraints (8):
    c: Coincident(g1,g-5)
    c: Coincident(g0,g-3)
    c: Coincident(g2,g-4)
    c: Coincident(g3,g-6)
    c: Equal(g2,g0)
    c: Equal(g2,g1)
    c: Equal(g2,g3)
    c: Diameter(g2) = 6.5
FEATURE [PartDesign::Pocket] Pocket107
  BaseFeature = -> Pocket106
  Direction = (0,0,1)
  Length = 3.5
  Length2 = 100
  Profile = -> Sketch254
  Suppressed = false
  Type = 0
FEATURE [PartDesign::Body] Body086  label="pince_cremaillere_pignon001"
  AllowCompound = false
  BaseFeature = -> InvoluteGear001
  Group = -> [BaseFeature003,Sketch253,Pocket106,Sketch254,Pocket107]
  Origin = -> Origin287
  Placement = pos=(25,20,27.098) rot=(0.715163,-0.698958,0;3.14159rad)
  Tip = -> Pocket107
FEATURE [Sketcher::SketchObject] Sketch255
  ArcFitTolerance = 0
  FullyConstrained = true
  MakeInternals = false
  MapMode = 2
  sketch-geometry (25):
    g0: LineSegment StartX=0 StartY=50 StartZ=0 EndX=100 EndY=50 EndZ=0
    g1: LineSegment StartX=100 StartY=50 StartZ=0 EndX=100 EndY=0 EndZ=0
    g2: LineSegment StartX=100 StartY=0 StartZ=0 EndX=0 EndY=0 EndZ=0
    g3: LineSegment StartX=0 StartY=0 StartZ=0 EndX=0 EndY=50 EndZ=0
    g4: Circle CenterX=50 CenterY=25 CenterZ=0 NormalX=0 NormalY=0 NormalZ=1 AngleXU=0 Radius=14
    g5: LineSegment [constr] StartX=0 StartY=50 StartZ=0 EndX=100 EndY=0 EndZ=0
    g6: LineSegment [constr] StartX=0 StartY=0 StartZ=0 EndX=100 EndY=50 EndZ=0
    g7: LineSegment [constr] StartX=29 StartY=41 StartZ=0 EndX=71 EndY=41 EndZ=0
    g8: LineSegment [constr] StartX=71 StartY=41 StartZ=0 EndX=71 EndY=9 EndZ=0
    g9: LineSegment [constr] StartX=71 StartY=9 StartZ=0 EndX=29 EndY=9 EndZ=0
    g10: LineSegment [constr] StartX=29 StartY=9 StartZ=0 EndX=29 EndY=41 EndZ=0
    g11: Circle CenterX=29 CenterY=41 CenterZ=0 NormalX=0 NormalY=0 NormalZ=1 AngleXU=0 Radius=1.75
    g12: Circle CenterX=71 CenterY=41 CenterZ=0 NormalX=0 NormalY=0 NormalZ=1 AngleXU=0 Radius=1.75
    g13: Circle CenterX=71 CenterY=9 CenterZ=0 NormalX=0 NormalY=0 NormalZ=1 AngleXU=0 Radius=1.75
    g14: Circle CenterX=29 CenterY=9 CenterZ=0 NormalX=0 NormalY=0 NormalZ=1 AngleXU=0 Radius=1.75
    g15: LineSegment [constr] StartX=0 StartY=25 StartZ=0 EndX=100 EndY=25 EndZ=0
    g16: LineSegment [constr] StartX=50 StartY=50 StartZ=0 EndX=50 EndY=0 EndZ=0
    g17: LineSegment [constr] StartX=3.5 StartY=33.25 StartZ=0 EndX=96.5 EndY=33.25 EndZ=0
    g18: LineSegment [constr] StartX=96.5 StartY=33.25 StartZ=0 EndX=96.5 EndY=16.75 EndZ=0
    g19: LineSegment [constr] StartX=96.5 StartY=16.75 StartZ=0 EndX=3.5 EndY=16.75 EndZ=0
    g20: LineSegment [constr] StartX=3.5 StartY=16.75 StartZ=0 EndX=3.5 EndY=33.25 EndZ=0
    g21: Circle CenterX=96.5 CenterY=33.25 CenterZ=0 NormalX=0 NormalY=0 NormalZ=1 AngleXU=0 Radius=1.65
    g22: Circle CenterX=3.5 CenterY=33.25 CenterZ=0 NormalX=0 NormalY=0 NormalZ=1 AngleXU=0 Radius=1.65
    g23: Circle CenterX=3.5 CenterY=16.75 CenterZ=0 NormalX=0 NormalY=0 NormalZ=1 AngleXU=0 Radius=1.65
    g24: Circle CenterX=96.5 CenterY=16.75 CenterZ=0 NormalX=0 NormalY=0 NormalZ=1 AngleXU=0 Radius=1.65
  constraints (60):
    c: Coincident(g0,g1)
    c: Coincident(g1,g2)
    c: Coincident(g2,g3)
    c: Coincident(g3,g0)
    c: Horizontal(g0)
    c: Horizontal(g2)
    c: Vertical(g1)
    c: Vertical(g3)
    c: Coincident(g2,g-1)
    c: Coincident(g5,g0)
    c: Coincident(g2,g6)
    c: Coincident(g0,g6)
    c: Coincident(g1,g5)
    c: PointOnObject(g4,g6)
    c: PointOnObject(g4,g5)
    c: Diameter(g4) = 28
    c: DistanceY(g3,g3) = 50
    c: DistanceX(g2,g2) = 100
    c: Coincident(g7,g8)
    c: Coincident(g8,g9)
    c: Coincident(g9,g10)
    c: Coincident(g10,g7)
    c: Horizontal(g7)
    c: Vertical(g10)
    c: Coincident(g11,g7)
    c: Coincident(g7,g12)
    c: Coincident(g9,g14)
    c: Coincident(g8,g13)
    c: Equal(g11,g12)
    c: Equal(g11,g14)
    c: Equal(g11,g13)
    c: Radius(g11) = 1.75
    c: DistanceY(g10,g10) = 32
    c: DistanceX(g7,g7) = 42
    c: PointOnObject(g16,g0)
    c: PointOnObject(g15,g1)
    c: PointOnObject(g15,g3)
    c: PointOnObject(g16,g2)
    c: Symmetric(g0,g0,g16)
    c: Symmetric(g0,g2,g15)
    c: Symmetric(g14,g13,g16)
    c: Symmetric(g12,g13,g15)
    c: Coincident(g17,g18)
    c: Coincident(g18,g19)
    c: Coincident(g19,g20)
    c: Coincident(g20,g17)
    c: Horizontal(g19)
    c: Vertical(g20)
    c: Symmetric(g17,g18,g15)
    c: Symmetric(g17,g17,g16)
    c: Distance(g20) = 16.5
    c: DistanceX(g0,g17) = 3.5
    c: Coincident(g24,g18)
    c: Coincident(g21,g17)
    c: Coincident(g17,g22)
    c: Coincident(g19,g23)
    c: Equal(g22,g23)
    c: Equal(g22,g21)
    c: Equal(g22,g24)
    c: Diameter(g22) = 3.3
FEATURE [PartDesign::Pad] Pad122
  AlongSketchNormal = false
  Direction = (0,0,1)
  Length = 8
  Length2 = 100
  Profile = -> Sketch255
  Suppressed = false
  Type = 0
FEATURE [Sketcher::SketchObject] Sketch256
  ArcFitTolerance = 0
  AttachmentSupport = -> [Pad122]
  ExternalGeometry = -> [Pad122]
  FullyConstrained = true
  MakeInternals = false
  MapMode = 5
  Placement = pos=(0,0,8) rot=(0,0,1;0rad)
  sketch-geometry (9):
    g0: LineSegment StartX=0 StartY=48 StartZ=0 EndX=100 EndY=48 EndZ=0
    g1: LineSegment StartX=100 StartY=48 StartZ=0 EndX=100 EndY=35.75 EndZ=0
    g2: LineSegment StartX=100 StartY=35.75 StartZ=0 EndX=0 EndY=35.75 EndZ=0
    g3: LineSegment StartX=0 StartY=35.75 StartZ=0 EndX=0 EndY=48 EndZ=0
    g4: LineSegment StartX=0 StartY=2 StartZ=0 EndX=100 EndY=2 EndZ=0
    g5: LineSegment StartX=100 StartY=2 StartZ=0 EndX=100 EndY=14.25 EndZ=0
    g6: LineSegment StartX=100 StartY=14.25 StartZ=0 EndX=0 EndY=14.25 EndZ=0
    g7: LineSegment StartX=0 StartY=14.25 StartZ=0 EndX=0 EndY=2 EndZ=0
    g8: Circle [constr] CenterX=50 CenterY=25 CenterZ=0 NormalX=0 NormalY=0 NormalZ=1 AngleXU=0 Radius=10.75
  constraints (26):
    c: Coincident(g0,g1)
    c: Coincident(g1,g2)
    c: Coincident(g2,g3)
    c: Coincident(g3,g0)
    c: Horizontal(g0)
    c: Horizontal(g2)
    c: Vertical(g1)
    c: Vertical(g3)
    c: Coincident(g4,g5)
    c: Coincident(g5,g6)
    c: Coincident(g6,g7)
    c: Coincident(g7,g4)
    c: Horizontal(g4)
    c: Horizontal(g6)
    c: Vertical(g5)
    c: Vertical(g7)
    c: PointOnObject(g6,g-6)
    c: PointOnObject(g2,g-6)
    c: PointOnObject(g1,g-5)
    c: PointOnObject(g5,g-5)
    c: Coincident(g8,g-7)
    c: Diameter(g8) = 21.5
    c: Tangent(g8,g2)
    c: Tangent(g6,g8)
    c: Equal(g7,g3)
    c: DistanceY(g0,g-6) = 2
FEATURE [PartDesign::Pocket] Pocket108
  BaseFeature = -> Pad122
  Direction = (0,0,-1)
  Length = 4
  Length2 = 100
  Profile = -> Sketch256
  Suppressed = false
  Type = 0
FEATURE [Sketcher::SketchObject] Sketch257
  ArcFitTolerance = 0
  AttachmentSupport = -> [Pocket108]
  ExternalGeometry = -> [Pocket108]
  FullyConstrained = true
  MakeInternals = false
  MapMode = 5
  Placement = pos=(0,0,8) rot=(0,0,1;0rad)
  sketch-geometry (10):
    g0: ArcOfCircle CenterX=11 CenterY=25 CenterZ=0 NormalX=0 NormalY=0 NormalZ=1 AngleXU=0 Radius=8 StartAngle=1.5708 EndAngle=4.71239
    g1: ArcOfCircle CenterX=26 CenterY=25 CenterZ=0 NormalX=0 NormalY=0 NormalZ=1 AngleXU=0 Radius=8 StartAngle=4.71239 EndAngle=7.85398
    g2: LineSegment StartX=11 StartY=17 StartZ=0 EndX=26 EndY=17 EndZ=0
    g3: LineSegment StartX=26 StartY=33 StartZ=0 EndX=11 EndY=33 EndZ=0
    g4: ArcOfCircle CenterX=74 CenterY=25 CenterZ=0 NormalX=0 NormalY=0 NormalZ=1 AngleXU=0 Radius=8 StartAngle=1.5708 EndAngle=4.71239
    g5: ArcOfCircle CenterX=89 CenterY=25 CenterZ=0 NormalX=0 NormalY=0 NormalZ=1 AngleXU=0 Radius=8 StartAngle=4.71239 EndAngle=7.85398
    g6: LineSegment StartX=74 StartY=17 StartZ=0 EndX=89 EndY=17 EndZ=0
    g7: LineSegment StartX=89 StartY=33 StartZ=0 EndX=74 EndY=33 EndZ=0
    g8: LineSegment [constr] StartX=50 StartY=50 StartZ=0 EndX=50 EndY=0 EndZ=0
    g9: LineSegment [constr] StartX=0 StartY=25 StartZ=0 EndX=100 EndY=25 EndZ=0
  constraints (26):
    c: Tangent(g0,g2) = -1.5708
    c: Tangent(g2,g1) = -1.5708
    c: Tangent(g1,g3) = -1.5708
    c: Tangent(g3,g0) = -1.5708
    c: Equal(g0,g1)
    c: Tangent(g4,g6) = -1.5708
    c: Tangent(g6,g5) = -1.5708
    c: Tangent(g5,g7) = -1.5708
    c: Tangent(g7,g4) = -1.5708
    c: Equal(g4,g5)
    c: PointOnObject(g-7,g9)
    c: PointOnObject(g-7,g8)
    c: PointOnObject(g8,g-6)
    c: PointOnObject(g8,g-5)
    c: PointOnObject(g9,g-3)
    c: PointOnObject(g9,g-4)
    c: Horizontal(g9)
    c: Vertical(g8)
    c: PointOnObject(g0,g9)
    c: PointOnObject(g1,g9)
    c: Symmetric(g1,g4,g8)
    c: Symmetric(g5,g0,g8)
    c: Equal(g1,g4)
    c: DistanceX(g-3,g0) = 11
    c: DistanceX(g1,g8) = 24
    c: DistanceY(g-7,g1) = 8
FEATURE [PartDesign::Pocket] Pocket109
  BaseFeature = -> Pocket108
  Direction = (0,0,-1)
  Length = 5
  Length2 = 100
  Profile = -> Sketch257
  Suppressed = false
  Type = 1
FEATURE [Sketcher::SketchObject] Sketch258
  ArcFitTolerance = 0
  AttachmentSupport = -> [Pocket109]
  ExternalGeometry = -> [Pocket109]
  FullyConstrained = true
  MakeInternals = false
  MapMode = 5
  Placement = pos=(0,0,4) rot=(0,0,1;0rad)
  sketch-geometry (4):
    g0: Circle CenterX=29 CenterY=41 CenterZ=0 NormalX=0 NormalY=0 NormalZ=1 AngleXU=0 Radius=3.5
    g1: Circle CenterX=71 CenterY=41 CenterZ=0 NormalX=0 NormalY=0 NormalZ=1 AngleXU=0 Radius=3.5
    g2: Circle CenterX=29 CenterY=9 CenterZ=0 NormalX=0 NormalY=0 NormalZ=1 AngleXU=0 Radius=3.5
    g3: Circle CenterX=71 CenterY=9 CenterZ=0 NormalX=0 NormalY=0 NormalZ=1 AngleXU=0 Radius=3.5
  constraints (8):
    c: Coincident(g-3,g0)
    c: Coincident(g1,g-4)
    c: Coincident(g2,g-5)
    c: Coincident(g3,g-6)
    c: Equal(g0,g1)
    c: Equal(g0,g2)
    c: Equal(g0,g3)
    c: Diameter(g0) = 7
FEATURE [PartDesign::Pocket] Pocket110
  BaseFeature = -> Pocket109
  Direction = (0,0,-1)
  Length = 2
  Length2 = 100
  Profile = -> Sketch258
  Suppressed = false
  Type = 0
FEATURE [PartDesign::Body] Body087  label="pince_support_cremaillere001"
  AllowCompound = false
  Group = -> [Sketch255,Pad122,Sketch256,Pocket108,Sketch257,Pocket109,Sketch258,Pocket110]
  Origin = -> Origin288
  Placement = pos=(-25,-5,20) rot=(0,0,1;0rad)
  Tip = -> Pocket110
FEATURE [Sketcher::SketchObject] Sketch259
  ArcFitTolerance = 1e-06
  AttachmentSupport = -> [XZ_Plane286]
  FullyConstrained = true
  MakeInternals = false
  MapMode = 5
  Placement = pos=(0,0,0) rot=(1,0,0;1.5708rad)
  sketch-geometry (4):
    g0: LineSegment StartX=-4.5 StartY=0 StartZ=0 EndX=4.5 EndY=0 EndZ=0
    g1: LineSegment StartX=4.5 StartY=0 StartZ=0 EndX=4.5 EndY=3 EndZ=0
    g2: LineSegment StartX=4.5 StartY=3 StartZ=0 EndX=-4.5 EndY=3 EndZ=0
    g3: LineSegment StartX=-4.5 StartY=3 StartZ=0 EndX=-4.5 EndY=0 EndZ=0
  constraints (11):
    c: Coincident(g0,g1)
    c: Coincident(g1,g2)
    c: Coincident(g2,g3)
    c: Coincident(g3,g0)
    c: Horizontal(g0)
    c: Vertical(g1)
    c: Vertical(g3)
    c: PointOnObject(g0,g-1)
    c: Symmetric(g1,g2,g-2)
    c: Distance(g2,g2) = 9
    c: DistanceY(g3,g3) = 3
FEATURE [PartDesign::Pad] Pad123
  Direction = (0,-1,2e-16)
  Length = 40
  Length2 = 10
  Midplane = true
  Placement = pos=(0,0,0) rot=(1,0,0;1.5708rad)
  Profile = -> Sketch259
  ReferenceAxis = -> Sketch259 [N_Axis]
  Suppressed = false
  Type = 0
FEATURE [PartDesign::Body] Body088  label="mousse002"
  AllowCompound = false
  Group = -> [Sketch259,Pad123]
  Origin = -> Origin289
  Placement = pos=(71.5056,23,59.5) rot=(0.707107,0,0.707107;3.14159rad)
  Tip = -> Pad123
FEATURE [Sketcher::SketchObject] Sketch260
  ArcFitTolerance = 0
  AttachmentSupport = -> [XZ_Plane288]
  FullyConstrained = true
  MakeInternals = false
  MapMode = 5
  Placement = pos=(0,0,0) rot=(1,0,0;1.5708rad)
  expr: Constraints[19] = 19.8 / 2
  sketch-geometry (8):
    g0: LineSegment StartX=2.5 StartY=3.4 StartZ=0 EndX=2.5 EndY=0 EndZ=0
    g1: LineSegment StartX=2.5 StartY=0 StartZ=0 EndX=4.2 EndY=0 EndZ=0
    g2: LineSegment StartX=4.2 StartY=0 StartZ=0 EndX=4.2 EndY=2 EndZ=0
    g3: LineSegment StartX=4.2 StartY=2 StartZ=0 EndX=9.9 EndY=2 EndZ=0
    g4: LineSegment StartX=9.9 StartY=2 StartZ=0 EndX=9.9 EndY=4.4 EndZ=0
    g5: LineSegment StartX=9.9 StartY=4.4 StartZ=0 EndX=1.5 EndY=4.4 EndZ=0
    g6: LineSegment StartX=1.5 StartY=4.4 StartZ=0 EndX=1.5 EndY=3.4 EndZ=0
    g7: LineSegment StartX=1.5 StartY=3.4 StartZ=0 EndX=2.5 EndY=3.4 EndZ=0
  constraints (24):
    c: PointOnObject(g0,g-1)
    c: Vertical(g0)
    c: Coincident(g1,g0)
    c: PointOnObject(g1,g-1)
    c: Coincident(g2,g1)
    c: Vertical(g2)
    c: Coincident(g3,g2)
    c: Horizontal(g3)
    c: Coincident(g4,g3)
    c: Vertical(g4)
    c: Coincident(g5,g4)
    c: Horizontal(g5)
    c: Coincident(g6,g5)
    c: Coincident(g7,g6)
    c: Coincident(g7,g0)
    c: Horizontal(g7)
    c: Vertical(g6)
    c: DistanceY(g4,g4) = 2.4
    c: DistanceY(g2,g2) = 2
    c: DistanceX(g-1,g4) = 9.9
    c: DistanceX(g-1,g6) = 1.5
    c: DistanceY(g0,g0) = 3.4
    c: DistanceX(g-1,g0) = 2.5
    c: DistanceX(g1,g1) = 1.7
FEATURE [PartDesign::Revolution] Revolution002
  Angle = 360
  Angle2 = 60
  Axis = (0,2e-16,1)
  Base = (0,0,0)
  Placement = pos=(0,0,0) rot=(1,0,0;1.5708rad)
  Profile = -> Sketch260
  ReferenceAxis = -> Sketch260 [V_Axis]
  Reversed = true
  Suppressed = false
  Type = 0
FEATURE [Sketcher::SketchObject] Sketch261
  ArcFitTolerance = 0
  AttachmentSupport = -> [XY_Plane288]
  FullyConstrained = true
  MakeInternals = false
  MapMode = 5
  sketch-geometry (1):
    g0: Circle CenterX=-7 CenterY=0 CenterZ=0 NormalX=0 NormalY=0 NormalZ=1 AngleXU=0 Radius=1.2
  constraints (3):
    c: PointOnObject(g0,g-1)
    c: Diameter(g0) = 2.4
    c: DistanceX(g0,g-1) = 7
FEATURE [PartDesign::Pocket] Pocket111
  BaseFeature = -> Revolution002
  Direction = (0,0,-1)
  Length = 5
  Length2 = 5
  Midplane = true
  Placement = pos=(0,0,0) rot=(1,0,0;1.5708rad)
  Profile = -> Sketch261
  ReferenceAxis = -> Sketch261 [N_Axis]
  Suppressed = false
  Type = 1
FEATURE [PartDesign::PolarPattern] PolarPattern006
  Angle = 360
  Axis = -> Sketch261 [N_Axis]
  BaseFeature = -> Pocket111
  Mode = 0
  Occurrences = 4
  Offset = 120
  Originals = -> [Pocket111]
  Placement = pos=(0,0,0) rot=(1,0,0;1.5708rad)
  Suppressed = false
  TransformMode = 0
FEATURE [PartDesign::Body] Body010  label="Corps002"
  AllowCompound = false
  Group = -> [Sketch260,Revolution002,Sketch261,Pocket111,PolarPattern006]
  Origin = -> Origin291
  Placement = pos=(0,0,0.4) rot=(0,0,1;0rad)
  Tip = -> PolarPattern006
FEATURE [App::Part] Part002004  label="servo_DS3218MG003"
  Group = -> [Part__Feature003,Part__Feature004,Part__Feature005,Body010,Screw005]
  Origin = -> Origin290
  Placement = pos=(25,20,15.9) rot=(0,0,1;4.71239rad)
FEATURE [Sketcher::SketchObject] Sketch262
  ArcFitTolerance = 1e-06
  AttachmentOffset = pos=(0,0,-10.75) rot=(0,0,1;0rad)
  AttachmentSupport = -> [YZ_Plane282]
  ExternalGeometry = -> [Pad119]
  FullyConstrained = true
  MakeInternals = false
  MapMode = 5
  Placement = pos=(-10.75,0,0) rot=(0.57735,0.57735,0.57735;2.0944rad)
  sketch-geometry (3):
    g0: LineSegment StartX=67.677 StartY=3 StartZ=0 EndX=92.677 EndY=9 EndZ=0
    g1: LineSegment StartX=67.677 StartY=3 StartZ=0 EndX=92.677 EndY=3 EndZ=0
    g2: LineSegment StartX=92.677 StartY=9 StartZ=0 EndX=92.677 EndY=3 EndZ=0
  constraints (8):
    c: PointOnObject(g0,g-4)
    c: Coincident(g1,g0)
    c: Coincident(g1,g-4)
    c: Coincident(g2,g0)
    c: Coincident(g2,g1)
    c: DistanceX(g1,g1) = 25
    c: Vertical(g2)
    c: DistanceY(g2,g2) = 6
FEATURE [PartDesign::Pad] Pad124
  BaseFeature = -> Pad119
  Direction = (1,0,0)
  Length = 5
  Length2 = 10
  Profile = -> Sketch262
  ReferenceAxis = -> Sketch262 [N_Axis]
  Suppressed = false
  Type = 0
FEATURE [PartDesign::Body] Body084  label="pince_cremaillere_bras002"
  AllowCompound = false
  BaseFeature = -> InvoluteRack001
  Group = -> [BaseFeature002,Sketch244,Pad119,Sketch262,Pad124]
  Origin = -> Origin285
  Placement = pos=(-18.1714,32.25,24) rot=(0,0,-1;1.5708rad)
  Tip = -> Pad124
FEATURE [Sketcher::SketchObject] Sketch263
  ArcFitTolerance = 1e-06
  AttachmentSupport = -> [YZ_Plane289]
  FullyConstrained = true
  MakeInternals = false
  MapMode = 5
  Placement = pos=(0,0,0) rot=(0.57735,0.57735,0.57735;2.0944rad)
  sketch-geometry (20):
    g0: LineSegment StartX=-16.6 StartY=41.5 StartZ=0 EndX=-16.6 EndY=39.5 EndZ=0
    g1: LineSegment StartX=-14.6 StartY=37.5 StartZ=0 EndX=-8.6 EndY=37.5 EndZ=0
    g2: LineSegment StartX=-6.6 StartY=35.5 StartZ=0 EndX=-6.6 EndY=-4.1 EndZ=0
    g3: LineSegment StartX=-4.6 StartY=-6.1 StartZ=0 EndX=0 EndY=-6.1 EndZ=0
    g4: LineSegment StartX=0 StartY=-6.1 StartZ=0 EndX=0 EndY=-0.1 EndZ=0
    g5: LineSegment StartX=0 StartY=-0.1 StartZ=0 EndX=-4.6 EndY=-0.1 EndZ=0
    g6: LineSegment StartX=-4.6 StartY=-0.1 StartZ=0 EndX=-4.6 EndY=6.6 EndZ=0
    g7: LineSegment StartX=-4.6 StartY=6.6 StartZ=0 EndX=0 EndY=6.6 EndZ=0
    g8: LineSegment StartX=0 StartY=6.6 StartZ=0 EndX=0 EndY=41.5 EndZ=0
    g9: LineSegment StartX=0 StartY=41.5 StartZ=0 EndX=-16.6 EndY=41.5 EndZ=0
    g10: ArcOfCircle CenterX=-8.6 CenterY=35.5 CenterZ=0 NormalX=0 NormalY=0 NormalZ=1 AngleXU=0 Radius=2 StartAngle=0 EndAngle=1.5708
    g11: GeomPoint [constr] X=-6.6 Y=37.5 Z=0
    g12: ArcOfCircle CenterX=-4.6 CenterY=-4.1 CenterZ=0 NormalX=0 NormalY=0 NormalZ=1 AngleXU=0 Radius=2 StartAngle=3.14159 EndAngle=4.71239
    g13: GeomPoint [constr] X=-6.6 Y=-6.1 Z=0
    g14: ArcOfCircle CenterX=-14.6 CenterY=39.5 CenterZ=0 NormalX=0 NormalY=0 NormalZ=1 AngleXU=0 Radius=2 StartAngle=3.14159 EndAngle=4.71239
    g15: GeomPoint [constr] X=-16.6 Y=37.5 Z=0
    g16: LineSegment [constr] StartX=-4.5 StartY=6.5 StartZ=0 EndX=-4.5 EndY=0 EndZ=0
    g17: LineSegment [constr] StartX=-4.5 StartY=0 StartZ=0 EndX=0 EndY=0 EndZ=0
    g18: LineSegment [constr] StartX=0 StartY=0 StartZ=0 EndX=0 EndY=6.5 EndZ=0
    g19: LineSegment [constr] StartX=0 StartY=6.5 StartZ=0 EndX=-4.5 EndY=6.5 EndZ=0
  constraints (53):
    c: Vertical(g0)
    c: Horizontal(g1)
    c: Vertical(g2)
    c: PointOnObject(g3,g-2)
    c: Horizontal(g3)
    c: Coincident(g3,g4)
    c: PointOnObject(g4,g-2)
    c: Coincident(g4,g5)
    c: Horizontal(g5)
    c: Vertical(g6)
    c: Coincident(g6,g7)
    c: Horizontal(g7)
    c: Coincident(g7,g8)
    c: Vertical(g8)
    c: Coincident(g8,g9)
    c: Coincident(g9,g0)
    c: Horizontal(g9)
    c: PointOnObject(g7,g-2)
    c: PointOnObject(g11,g1)
    c: PointOnObject(g11,g2)
    c: Tangent(g1,g10) = 1.5708
    c: Tangent(g2,g10) = 1.5708
    c: PointOnObject(g13,g3)
    c: PointOnObject(g13,g2)
    c: Tangent(g3,g12) = -1.5708
    c: Tangent(g2,g12) = -1.5708
    c: PointOnObject(g15,g1)
    c: PointOnObject(g15,g0)
    c: Tangent(g1,g14) = -1.5708
    c: Tangent(g0,g14) = -1.5708
    c: DistanceY(g1,g0) = 4
    c: DistanceX(g0,g2) = 10
    c: Equal(g14,g10)
    c: Radius(g14) = 2
    c: Coincident(g16,g17)
    c: Coincident(g17,g18)
    c: Coincident(g18,g19)
    c: Coincident(g19,g16)
    c: Vertical(g16)
    c: Vertical(g18)
    c: Horizontal(g17)
    c: Horizontal(g19)
    c: Coincident(g17,g-1)
    c: DistanceX(g6,g16) = 0.1
    c: DistanceY(g18,g7) = 0.1
    c: DistanceX(g17,g17) = 4.5
    c: DistanceY(g18,g18) = 6.5
    c: DistanceY(g-1,g8) = 41.5
    c: DistanceY(g4,g4) = 6
    c: DistanceY(g4,g17) = 0.1
    c: Coincident(g5,g6)
    c: Vertical(g12,g5)
    c: Radius(g12) = 2
FEATURE [PartDesign::Pad] Pad125
  Direction = (1,0,0)
  Length = 20
  Length2 = 10
  Midplane = true
  Placement = pos=(0,0,0) rot=(1,1,1;2.0944rad)
  Profile = -> Sketch263
  ReferenceAxis = -> Sketch263 [N_Axis]
  Suppressed = false
  Type = 0
FEATURE [Sketcher::SketchObject] Sketch264
  ArcFitTolerance = 1e-06
  AttachmentSupport = -> [XY_Plane289]
  ExternalGeometry = -> [Pad125]
  FullyConstrained = true
  MakeInternals = false
  MapMode = 5
  Placement = pos=(0,0,0) rot=(0,1,0;3.14159rad)
  sketch-geometry (8):
    g0: Circle CenterX=0 CenterY=-11.6 CenterZ=0 NormalX=0 NormalY=0 NormalZ=1 AngleXU=0 Radius=2.75
    g1: LineSegment [constr] StartX=-5e-16 StartY=-8.6 StartZ=0 EndX=5e-16 EndY=-14.6 EndZ=0
    g2: LineSegment [constr] StartX=4 StartY=-9.6 StartZ=0 EndX=4 EndY=-16.6 EndZ=0
    g3: LineSegment [constr] StartX=4 StartY=-16.6 StartZ=0 EndX=10 EndY=-16.6 EndZ=0
    g4: LineSegment [constr] StartX=10 StartY=-16.6 StartZ=0 EndX=10 EndY=-8.6 EndZ=0
    g5: LineSegment [constr] StartX=10 StartY=-8.6 StartZ=0 EndX=5 EndY=-8.6 EndZ=0
    g6: ArcOfCircle [constr] CenterX=5 CenterY=-9.6 CenterZ=0 NormalX=0 NormalY=0 NormalZ=1 AngleXU=0 Radius=1 StartAngle=1.5708 EndAngle=3.14159
    g7: GeomPoint [constr] X=4 Y=-8.6 Z=0
  constraints (21):
    c: PointOnObject(g1,g-3)
    c: PointOnObject(g1,g-4)
    c: Perpendicular(g-3,g1)
    c: Symmetric(g1,g1,g0)
    c: Diameter(g0) = 5.5
    c: Coincident(g2,g3)
    c: Coincident(g3,g4)
    c: Coincident(g4,g5)
    c: Vertical(g2)
    c: Vertical(g4)
    c: Horizontal(g3)
    c: Horizontal(g5)
    c: Coincident(g3,g-5)
    c: PointOnObject(g7,g5)
    c: PointOnObject(g7,g2)
    c: Tangent(g5,g6) = -1.5708
    c: Tangent(g2,g6) = -1.5708
    c: PointOnObject(g7,g-3)
    c: Radius(g6) = 1
    c: DistanceX(g0,g2) = 4
    c: PointOnObject(g0,g-2)
FEATURE [PartDesign::Pocket] Pocket112
  BaseFeature = -> Pad125
  Direction = (0,0,1)
  Length = 5
  Length2 = 5
  Placement = pos=(0,0,0) rot=(1,1,1;2.0944rad)
  Profile = -> Sketch264
  ReferenceAxis = -> Sketch264 [N_Axis]
  Suppressed = false
  Type = 1
FEATURE [Sketcher::SketchObject] Sketch265
  ArcFitTolerance = 1e-06
  AttachmentOffset = pos=(0,0,-6) rot=(0,0,1;0rad)
  AttachmentSupport = -> [Pocket112]
  FullyConstrained = true
  MakeInternals = false
  MapMode = 5
  Placement = pos=(0,-1.3e-15,-0.1) rot=(0.707107,0.707107,0;3.14159rad)
  sketch-geometry (1):
    g0: Circle CenterX=0 CenterY=-3.5 CenterZ=0 NormalX=0 NormalY=0 NormalZ=1 AngleXU=0 Radius=2.1
  constraints (3):
    c: Diameter(g0) = 4.2
    c: PointOnObject(g0,g-2)
    c: DistanceY(g0,g-1) = 3.5
FEATURE [PartDesign::Pocket] Pocket113
  BaseFeature = -> Pocket112
  Direction = (0,0,1)
  Length = 16
  Length2 = 5
  Placement = pos=(0,0,0) rot=(1,1,1;2.0944rad)
  Profile = -> Sketch265
  ReferenceAxis = -> Sketch265 [N_Axis]
  Reversed = true
  Suppressed = false
  Type = 0
FEATURE [Sketcher::SketchObject] Sketch266
  ArcFitTolerance = 1e-06
  AttachmentSupport = -> [XZ_Plane289]
  ExternalGeometry = -> [Pocket113]
  FullyConstrained = true
  MakeInternals = false
  MapMode = 5
  Placement = pos=(0,0,0) rot=(1,0,0;1.5708rad)
  sketch-geometry (6):
    g0: LineSegment StartX=10 StartY=-6.1 StartZ=0 EndX=10 EndY=35.5 EndZ=0
    g1: LineSegment StartX=10 StartY=35.5 StartZ=0 EndX=2 EndY=-6.1 EndZ=0
    g2: LineSegment StartX=2 StartY=-6.1 StartZ=0 EndX=10 EndY=-6.1 EndZ=0
    g3: LineSegment StartX=-8 StartY=35 StartZ=0 EndX=4.5 EndY=22.5 EndZ=0
    g4: LineSegment StartX=4.5 StartY=22.5 StartZ=0 EndX=-8 EndY=10 EndZ=0
    g5: LineSegment StartX=-8 StartY=35 StartZ=0 EndX=-8 EndY=10 EndZ=0
  constraints (16):
    c: Coincident(g1,g2)
    c: Coincident(g2,g0)
    c: Horizontal(g2)
    c: Coincident(g0,g-4)
    c: Coincident(g0,g-3)
    c: Coincident(g0,g1)
    c: DistanceX(g2,g2) = 8
    c: Coincident(g4,g3)
    c: Coincident(g5,g3)
    c: Coincident(g5,g4)
    c: Vertical(g5)
    c: Angle(g5,g3) = 0.785398
    c: Equal(g3,g4)
    c: DistanceX(g3,g-1) = 8
    c: DistanceY(g-1,g3) = 35
    c: DistanceY(g5,g5) = 25
FEATURE [PartDesign::Pocket] Pocket114
  BaseFeature = -> Pocket113
  Direction = (0,1,-2e-16)
  Length = 5
  Length2 = 5
  Midplane = true
  Placement = pos=(0,0,0) rot=(1,1,1;2.0944rad)
  Profile = -> Sketch266
  ReferenceAxis = -> Sketch266 [N_Axis]
  Suppressed = false
  Type = 1
FEATURE [PartDesign::Mirrored] Mirrored011
  BaseFeature = -> Pocket114
  MirrorPlane = -> XZ_Plane289
  Originals = -> [Pocket114]
  Placement = pos=(0,0,0) rot=(1,1,1;2.0944rad)
  Refine = true
  Suppressed = false
  TransformMode = 1
FEATURE [Sketcher::SketchObject] Sketch
  ArcFitTolerance = 1e-06
  AttachmentSupport = -> [Mirrored011]
  FullyConstrained = true
  MakeInternals = false
  MapMode = 5
  Placement = pos=(0,-5.3e-15,6.6) rot=(0.707107,0.707107,0;3.14159rad)
  sketch-geometry (1):
    g0: Circle CenterX=0 CenterY=-3.5 CenterZ=0 NormalX=0 NormalY=0 NormalZ=1 AngleXU=0 Radius=3.25
  constraints (3):
    c: Diameter(g0) = 6.5
    c: PointOnObject(g0,g-2)
    c: DistanceY(g0,g-1) = 3.5
FEATURE [PartDesign::Pocket] Pocket
  BaseFeature = -> Mirrored011
  Direction = (0,0,1)
  Length = 5
  Length2 = 5
  Placement = pos=(0,0,0) rot=(1,1,1;2.0944rad)
  Profile = -> Sketch
  ReferenceAxis = -> Sketch [N_Axis]
  Suppressed = false
  Type = 1
FEATURE [PartDesign::Body] Body089  label="support_rail_haut001"
  AllowCompound = false
  Group = -> [Sketch263,Pad125,Sketch264,Pocket112,Sketch265,Pocket113,Sketch266,Pocket114,Mirrored011,Sketch,Pocket]
  Origin = -> Origin292
  Placement = pos=(0,-2e-15,218) rot=(-0.707107,0,-0.707107;3.14159rad)
  Tip = -> Pocket
FEATURE [Sketcher::SketchObject] Sketch267
  ArcFitTolerance = 1e-06
  AttachmentSupport = -> [XZ_Plane290]
  FullyConstrained = true
  MakeInternals = false
  MapMode = 5
  Placement = pos=(0,0,0) rot=(1,0,0;1.5708rad)
  sketch-geometry (4):
    g0: LineSegment StartX=-4.5 StartY=0 StartZ=0 EndX=4.5 EndY=0 EndZ=0
    g1: LineSegment StartX=4.5 StartY=0 StartZ=0 EndX=4.5 EndY=2 EndZ=0
    g2: LineSegment StartX=4.5 StartY=2 StartZ=0 EndX=-4.5 EndY=2 EndZ=0
    g3: LineSegment StartX=-4.5 StartY=2 StartZ=0 EndX=-4.5 EndY=0 EndZ=0
  constraints (11):
    c: Coincident(g0,g1)
    c: Coincident(g1,g2)
    c: Coincident(g2,g3)
    c: Coincident(g3,g0)
    c: Horizontal(g0)
    c: Vertical(g1)
    c: Vertical(g3)
    c: PointOnObject(g0,g-1)
    c: Symmetric(g1,g2,g-2)
    c: Distance(g2,g2) = 9
    c: DistanceY(g3,g3) = 2
FEATURE [PartDesign::Pad] Pad126
  Direction = (0,-1,2e-16)
  Length = 40
  Length2 = 10
  Midplane = true
  Placement = pos=(0,0,0) rot=(1,0,0;1.5708rad)
  Profile = -> Sketch267
  ReferenceAxis = -> Sketch267 [N_Axis]
  Suppressed = false
  Type = 0
FEATURE [PartDesign::Body] Body090  label="cale"
  AllowCompound = false
  Group = -> [Sketch267,Pad126]
  Origin = -> Origin293
  Placement = pos=(71.5056,23,59.5) rot=(0.707107,0,0.707107;3.14159rad)
  Tip = -> Pad126
FEATURE [Sketcher::SketchObject] Sketch215
  ArcFitTolerance = 1e-06
  AttachmentSupport = -> [XY_Plane291]
  FullyConstrained = true
  MakeInternals = false
  MapMode = 5
  expr: Constraints[2] = 16.5 mm / 2
  sketch-geometry (5):
    g0: Circle CenterX=-8.25 CenterY=0 CenterZ=0 NormalX=0 NormalY=0 NormalZ=1 AngleXU=0 Radius=2.1
    g1: ArcOfCircle CenterX=-8.25 CenterY=0 CenterZ=0 NormalX=0 NormalY=0 NormalZ=1 AngleXU=0 Radius=3 StartAngle=1.5708 EndAngle=4.71239
    g2: LineSegment StartX=0 StartY=-3 StartZ=0 EndX=-8.25 EndY=-3 EndZ=0
    g3: LineSegment StartX=0 StartY=3 StartZ=0 EndX=-8.25 EndY=3 EndZ=0
    g4: LineSegment StartX=0 StartY=3 StartZ=0 EndX=0 EndY=-3 EndZ=0
  constraints (13):
    c: Diameter(g0) = 4.2
    c: PointOnObject(g0,g-1)
    c: DistanceX(g0,g-1) = 8.25
    c: Tangent(g1,g2) = 1.5708
    c: Tangent(g1,g3) = -1.5708
    c: Horizontal(g3)
    c: Coincident(g1,g0)
    c: PointOnObject(g3,g-2)
    c: PointOnObject(g2,g-2)
    c: Coincident(g4,g3)
    c: Coincident(g4,g2)
    c: Horizontal(g2)
    c: Radius(g1) = 3
FEATURE [PartDesign::Pad] Pad110
  Direction = (0,0,1)
  Length = 15
  Length2 = 10
  Profile = -> Sketch215
  ReferenceAxis = -> Sketch215 [N_Axis]
  Suppressed = false
  Type = 0
FEATURE [Sketcher::SketchObject] Sketch216
  ArcFitTolerance = 1e-06
  AttachmentSupport = -> [XZ_Plane291]
  FullyConstrained = true
  MakeInternals = false
  MapMode = 5
  Placement = pos=(0,0,0) rot=(1,0,0;1.5708rad)
  sketch-geometry (6):
    g0: LineSegment StartX=-3.2536 StartY=15 StartZ=0 EndX=-3.11715 EndY=7.18255 EndZ=0
    g1: LineSegment StartX=0 StartY=6.2 StartZ=0 EndX=-2.1173 EndY=6.2 EndZ=0
    g2: LineSegment StartX=0 StartY=6.2 StartZ=0 EndX=0 EndY=15 EndZ=0
    g3: LineSegment StartX=-3.2536 StartY=15 StartZ=0 EndX=0 EndY=15 EndZ=0
    g4: ArcOfCircle CenterX=-2.1173 CenterY=7.2 CenterZ=0 NormalX=0 NormalY=0 NormalZ=1 AngleXU=0 Radius=1 StartAngle=3.15905 EndAngle=4.71239
    g5: GeomPoint [constr] X=-3.1 Y=6.2 Z=0
  constraints (16):
    c: PointOnObject(g1,g-2)
    c: Coincident(g2,g1)
    c: Vertical(g2)
    c: Coincident(g3,g0)
    c: Coincident(g3,g2)
    c: DistanceY(g-1,g1) = 6.2
    c: Horizontal(g3)
    c: DistanceY(g-1,g0) = 15
    c: Horizontal(g1)
    c: DistanceX(g5,g1) = 3.1
    c: PointOnObject(g5,g0)
    c: PointOnObject(g5,g1)
    c: Tangent(g0,g4) = -1.5708
    c: Tangent(g1,g4) = 1.5708
    c: Angle(g1,g0) = 1.58825
    c: Radius(g4) = 1
FEATURE [PartDesign::Pocket] Pocket079
  BaseFeature = -> Pad110
  Direction = (0,1,-2e-16)
  Length = 5
  Length2 = 5
  Midplane = true
  Profile = -> Sketch216
  ReferenceAxis = -> Sketch216 [N_Axis]
  Suppressed = false
  Type = 1
FEATURE [Sketcher::SketchObject] Sketch268
  ArcFitTolerance = 1e-06
  AttachmentSupport = -> [XZ_Plane291]
  ExternalGeometry = -> [Pocket079]
  FullyConstrained = true
  MakeInternals = false
  MapMode = 5
  Placement = pos=(0,0,0) rot=(1,0,0;1.5708rad)
  sketch-geometry (3):
    g0: LineSegment StartX=-12 StartY=8 StartZ=0 EndX=-5 EndY=15 EndZ=0
    g1: LineSegment StartX=-12 StartY=15 StartZ=0 EndX=-12 EndY=8 EndZ=0
    g2: LineSegment StartX=-5 StartY=15 StartZ=0 EndX=-12 EndY=15 EndZ=0
  constraints (9):
    c: Vertical(g1)
    c: Coincident(g1,g2)
    c: Coincident(g0,g2)
    c: Coincident(g0,g1)
    c: Horizontal(g2)
    c: Horizontal(g2,g-3)
    c: DistanceX(g1,g-1) = 12
    c: Angle(g0,g1) = 0.785398
    c: DistanceX(g2,g2) = 7
FEATURE [PartDesign::Pocket] Pocket115
  BaseFeature = -> Pocket079
  Direction = (0,1,-2e-16)
  Length = 5
  Length2 = 5
  Midplane = true
  Profile = -> Sketch268
  ReferenceAxis = -> Sketch268 [N_Axis]
  Suppressed = false
  Type = 1
FEATURE [PartDesign::Mirrored] Mirrored046
  BaseFeature = -> Pocket115
  MirrorPlane = -> Sketch216 [V_Axis]
  Originals = -> [Pocket079]
  Suppressed = false
  TransformMode = 1
FEATURE [PartDesign::Body] Body091  label="porte_cale"
  AllowCompound = false
  Group = -> [Sketch215,Pad110,Sketch216,Pocket079,Sketch268,Pocket115,Mirrored046]
  Origin = -> Origin294
  Placement = pos=(71.5,19.83,20) rot=(-0.707107,-0.707107,0;3.14159rad)
  Tip = -> Mirrored046
FEATURE [Assembly::AssemblyObject] Assembly002  label="Assembly_pince"
  Group = -> [Joints002,Part002004,Body083,InvoluteRack001,Body084,Body085,InvoluteGear001,Body086,Body087,Body088,Link004,Link005,GroundedJoint001,Joint001,Joint002,Joint003,Joint004,Joint005,Joint006,Joint007,Joint008,Joint009,Joint010,Body090,Body091]
  Origin = -> Origin283
  Placement = pos=(89,20,151.5) rot=(1,0,0;3.14159rad)
  Type = Assembly
FEATURE [App::Part] Part002003  label="Partie mobile"
  Group = -> [Part,Assembly002]
  Origin = -> Origin282
  Placement = pos=(0,0,6) rot=(0,0,1;0rad)
  expr: .Placement.Base.z = VarSet.Position_verrin + 6 mm
FEATURE [Assembly::AssemblyObject] Assembly001
  Group = -> [Joints001,L16_50MM_SW_ASM,Part002002,Body013,Body017,Body089,Body082,Part002003]
  Origin = -> Origin015
  Type = Assembly
